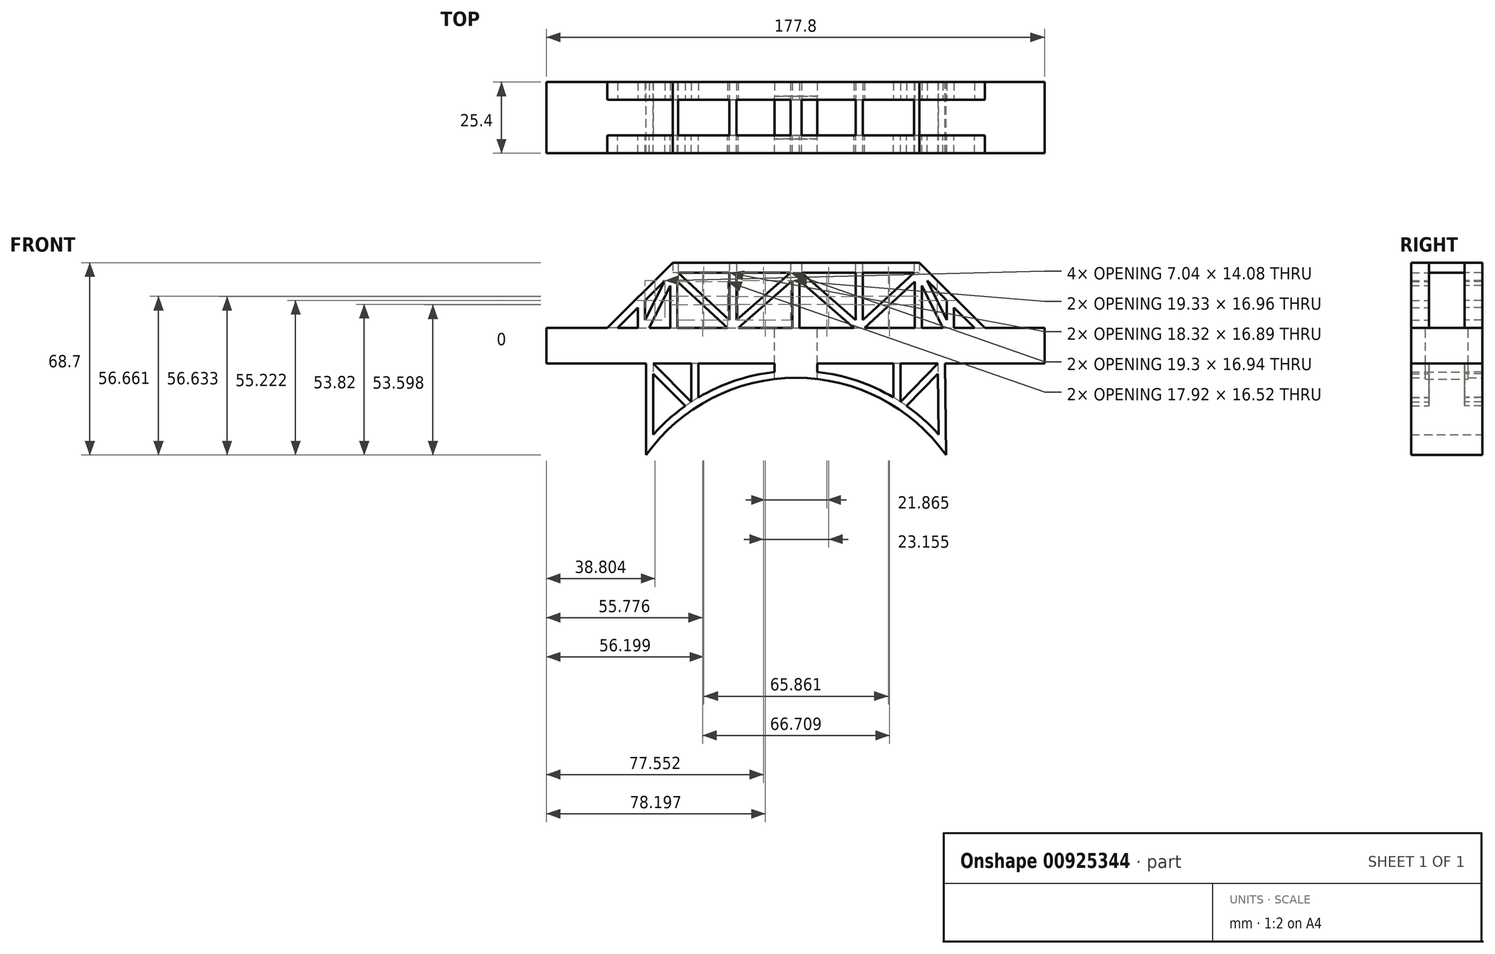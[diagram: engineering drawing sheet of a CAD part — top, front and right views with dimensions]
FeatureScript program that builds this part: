
annotation { "Feature Type Name" : "Feature", "Feature Type Description" : "" }
export const myFeature = defineFeature(function(context is Context, id is Id, definition is map)
    precondition{}
    {
        {
            var Q0;
            Q0=qCreatedBy(makeId("Front.planeOp"),FACE);
            var sketch = newSketch(context, id + "F0", { "sketchPlane" : qUnion([Q0])});
            skLineSegment(sketch, "E0.bottom", {"start": v(-63.73, 4.53) * mm, "end": v(63.73, 4.53) * mm});
            skLineSegment(sketch, "E1.bottom", {"start": v(-63.73, 4.53) * mm, "end": v(-89.13, 4.53) * mm});
            skLineSegment(sketch, "E1.top", {"start": v(-63.73, -8.17) * mm, "end": v(-89.13, -8.17) * mm});
            skLineSegment(sketch, "E1.left", {"start": v(-63.73, -3.37) * mm, "end": v(-63.73, -8.17) * mm});
            skLineSegment(sketch, "E1.right", {"start": v(-89.13, 4.53) * mm, "end": v(-89.13, -8.17) * mm});
            skPoint(sketch, "E2.oppositeSnap0", {"position": v(-76.43, -8.17) * mm});
            skLineSegment(sketch, "E2.bottom", {"start": v(63.27, 4.53) * mm, "end": v(88.67, 4.53) * mm});
            skLineSegment(sketch, "E2.left", {"start": v(63.27, 4.53) * mm, "end": v(63.27, -8.17) * mm});
            skLineSegment(sketch, "E2.right", {"start": v(88.67, 4.53) * mm, "end": v(88.67, -8.17) * mm});
            skPoint(sketch, "E3", {"position": v(-3.25, -27.46) * mm});
            skPoint(sketch, "E4", {"position": v(-24.97, -27.46) * mm});
            skPoint(sketch, "E5", {"position": v(18.48, -27.46) * mm});
            skPoint(sketch, "E6", {"position": v(0, -8.17) * mm});
            skPoint(sketch, "E7", {"position": v(-22.52, -8.17) * mm});
            skPoint(sketch, "E8", {"position": v(22.52, -8.17) * mm});
            skLineSegment(sketch, "E9", {"start": v(-43.58, -8.17) * mm, "end": v(-43.58, 4.53) * mm});
            skLineSegment(sketch, "E10", {"start": v(-22.52, -8.17) * mm, "end": v(-22.52, 4.53) * mm});
            skLineSegment(sketch, "E11", {"start": v(0, -8.17) * mm, "end": v(0, 4.53) * mm});
            skLineSegment(sketch, "E12", {"start": v(22.52, -8.17) * mm, "end": v(22.52, 4.53) * mm});
            skLineSegment(sketch, "E13", {"start": v(43.58, -8.17) * mm, "end": v(43.58, 4.53) * mm});
            skLineSegment(sketch, "E14", {"start": v(-63.73, 4.53) * mm, "end": v(-63.73, 4.53) * mm});
            skLineSegment(sketch, "E15", {"start": v(-63.73, -3.37) * mm, "end": v(-63.73, 4.53) * mm});
            skLineSegment(sketch, "E16", {"start": v(63.73, 4.53) * mm, "end": v(43.97, 24.3) * mm});
            skLineSegment(sketch, "E17", {"start": v(43.97, 24.3) * mm, "end": v(-43.97, 24.3) * mm});
            skLineSegment(sketch, "E18", {"start": v(-43.97, 24.3) * mm, "end": v(-63.73, 4.53) * mm});
            skLineSegment(sketch, "E19", {"start": v(-53.85, 14.41) * mm, "end": v(-53.85, 4.53) * mm});
            skLineSegment(sketch, "E20", {"start": v(-53.85, 4.53) * mm, "end": v(-43.97, 24.3) * mm});
            skLineSegment(sketch, "E21", {"start": v(53.85, 14.41) * mm, "end": v(53.85, 4.53) * mm});
            skLineSegment(sketch, "E22", {"start": v(43.97, 24.3) * mm, "end": v(53.85, 4.53) * mm});
            skLineSegment(sketch, "E23", {"start": v(43.97, 24.3) * mm, "end": v(22.52, 4.53) * mm});
            skLineSegment(sketch, "E24", {"start": v(0, 24.3) * mm, "end": v(22.52, 4.53) * mm});
            skLineSegment(sketch, "E25", {"start": v(-22.52, 4.53) * mm, "end": v(0, 24.3) * mm});
            skLineSegment(sketch, "E26", {"start": v(-43.97, 24.3) * mm, "end": v(-22.52, 4.53) * mm});
            skLineSegment(sketch, "E27.0", {"start": v(43.58, 22.22) * mm, "end": v(52.43, 4.53) * mm});
            skLineSegment(sketch, "E27.1", {"start": v(43.58, 22.22) * mm, "end": v(24.4, 4.53) * mm});
            skLineSegment(sketch, "E27.2", {"start": v(-52.43, 4.53) * mm, "end": v(-43.58, 22.22) * mm});
            skLineSegment(sketch, "E27.3", {"start": v(-43.58, 22.22) * mm, "end": v(-24.4, 4.53) * mm});
            skLineSegment(sketch, "E27.4", {"start": v(-20.6, 4.53) * mm, "end": v(0, 22.6) * mm});
            skLineSegment(sketch, "E27.5", {"start": v(0, 22.6) * mm, "end": v(20.6, 4.53) * mm});
            skLineSegment(sketch, "E28.0", {"start": v(42.1, 24.3) * mm, "end": v(22.5, 6.24) * mm});
            skLineSegment(sketch, "E28.1", {"start": v(1.93, 24.3) * mm, "end": v(22.5, 6.24) * mm});
            skLineSegment(sketch, "E28.2", {"start": v(-22.5, 6.24) * mm, "end": v(-1.93, 24.3) * mm});
            skLineSegment(sketch, "E28.3", {"start": v(-42.1, 24.3) * mm, "end": v(-22.5, 6.24) * mm});
            skLineSegment(sketch, "E29.0", {"start": v(-43.97, 27.89) * mm, "end": v(-67.32, 4.53) * mm});
            skLineSegment(sketch, "E30", {"start": v(-43.97, 27.89) * mm, "end": v(43.97, 27.89) * mm});
            skLineSegment(sketch, "E31.0", {"start": v(67.32, 4.53) * mm, "end": v(43.97, 27.89) * mm});
            skLineSegment(sketch, "E32", {"start": v(-43.58, 4.53) * mm, "end": v(-43.58, 22.22) * mm});
            skLineSegment(sketch, "E33", {"start": v(43.58, 22.22) * mm, "end": v(43.58, 4.53) * mm});
            skLineSegment(sketch, "E34", {"start": v(0, 22.6) * mm, "end": v(0, 4.53) * mm});
            skLineSegment(sketch, "E35", {"start": v(-22.5, 6.24) * mm, "end": v(-22.5, 24.3) * mm});
            skLineSegment(sketch, "E36", {"start": v(22.5, 6.24) * mm, "end": v(22.5, 24.3) * mm});
            skLineSegment(sketch, "E37.0", {"start": v(-21.23, 7.35) * mm, "end": v(-21.23, 24.3) * mm});
            skLineSegment(sketch, "E38.0", {"start": v(-23.77, 7.4) * mm, "end": v(-23.77, 24.3) * mm});
            skLineSegment(sketch, "E39.0", {"start": v(23.77, 7.4) * mm, "end": v(23.77, 24.3) * mm});
            skLineSegment(sketch, "E40.0", {"start": v(21.23, 7.35) * mm, "end": v(21.23, 24.3) * mm});
            skLineSegment(sketch, "E41.0", {"start": v(-42.31, 4.53) * mm, "end": v(-42.31, 21.05) * mm});
            skLineSegment(sketch, "E42.0", {"start": v(-44.85, 4.53) * mm, "end": v(-44.85, 19.68) * mm});
            skLineSegment(sketch, "E43.0", {"start": v(42.31, 21.05) * mm, "end": v(42.31, 4.53) * mm});
            skLineSegment(sketch, "E44.0", {"start": v(44.85, 19.68) * mm, "end": v(44.85, 4.53) * mm});
            skLineSegment(sketch, "E45", {"start": v(-23.77, 24.3) * mm, "end": v(-21.23, 24.3) * mm});
            skLineSegment(sketch, "E46", {"start": v(-23.77, 7.4) * mm, "end": v(-22.5, 6.24) * mm});
            skLineSegment(sketch, "E47", {"start": v(-22.5, 6.24) * mm, "end": v(-21.23, 7.35) * mm});
            skLineSegment(sketch, "E48.0", {"start": v(-1.27, 21.49) * mm, "end": v(-1.27, 4.52) * mm});
            skLineSegment(sketch, "E49.0", {"start": v(1.27, 21.49) * mm, "end": v(1.27, 4.52) * mm});
            skLineSegment(sketch, "E50.0", {"start": v(-56.39, 11.87) * mm, "end": v(-56.39, 4.53) * mm});
            skLineSegment(sketch, "E51.0", {"start": v(56.39, 11.87) * mm, "end": v(56.39, 4.53) * mm});
            skLineSegment(sketch, "E52.0", {"start": v(46.8, 21.45) * mm, "end": v(53.85, 7.37) * mm});
            skLineSegment(sketch, "E53", {"start": v(-7.62, -8.17) * mm, "end": v(-7.62, 4.53) * mm});
            skLineSegment(sketch, "E54", {"start": v(7.62, -8.17) * mm, "end": v(7.62, 4.53) * mm});
            skLineSegment(sketch, "E55.0", {"start": v(-53.85, 7.37) * mm, "end": v(-46.8, 21.45) * mm});
            skLineSegment(sketch, "E56", {"start": v(-51.03, -8.17) * mm, "end": v(-51.03, -33.57) * mm});
            skLineSegment(sketch, "E57", {"start": v(50.57, -8.17) * mm, "end": v(50.93, -33.45) * mm});
            skArc(sketch, "E58", {"start": v(50.93, -33.45) * mm, "mid": v(-0.08, -10.7) * mm, "end": v(-51.03, -33.57) * mm});
            skLineSegment(sketch, "E59.0", {"start": v(-53.57, -8.17) * mm, "end": v(-53.57, -40.8) * mm});
            skArc(sketch, "E59.1", {"start": v(53.57, -40.8) * mm, "mid": v(0, -13.25) * mm, "end": v(-53.57, -40.8) * mm});
            skLineSegment(sketch, "E59.2", {"start": v(53.1, -8.17) * mm, "end": v(53.57, -40.8) * mm});
            skLineSegment(sketch, "E60", {"start": v(-51.03, -8.17) * mm, "end": v(-37.37, -21.83) * mm});
            skLineSegment(sketch, "E61", {"start": v(-37.37, -21.83) * mm, "end": v(-37.37, -8.17) * mm});
            skLineSegment(sketch, "E62", {"start": v(37.32, -8.14) * mm, "end": v(37.32, -21.8) * mm});
            skLineSegment(sketch, "E63", {"start": v(37.32, -21.8) * mm, "end": v(50.57, -8.17) * mm});
            skLineSegment(sketch, "E64.0", {"start": v(34.78, -8.14) * mm, "end": v(34.78, -20.22) * mm});
            skLineSegment(sketch, "E65.0", {"start": v(39.46, -23.24) * mm, "end": v(50.62, -11.76) * mm});
            skLineSegment(sketch, "E66.0", {"start": v(-34.83, -20.25) * mm, "end": v(-34.83, -8.17) * mm});
            skLineSegment(sketch, "E67.0", {"start": v(-51.03, -11.76) * mm, "end": v(-39.51, -23.28) * mm});
            skLineSegment(sketch, "E68", {"start": v(-22.52, -8.17) * mm, "end": v(-17.66, -13.03) * mm});
            skLineSegment(sketch, "E69", {"start": v(22.52, -8.17) * mm, "end": v(17.66, -13.03) * mm});
            skLineSegment(sketch, "E70", {"start": v(-7.62, -8.17) * mm, "end": v(-7.62, -11.14) * mm});
            skLineSegment(sketch, "E71", {"start": v(7.62, -8.17) * mm, "end": v(7.62, -11.14) * mm});
            skLineSegment(sketch, "E72", {"start": v(88.67, -8.17) * mm, "end": v(-63.73, -8.17) * mm});
            skSolve(sketch);
        }
        {
            var Q0;
            Q0=makeQuery(id+"F0.imprint","IMPRINT",FACE,{"disambiguationData":[TD([[makeQuery(id+"F0.imprint","IMPRINT",EDGE,{"derivedFrom":sQuery(id+"F0.wireOp",EDGE,"E1.top")}),-1.0]])]});
            var Q1;
            {var subQ0=sQuery(id+"F0.wireOp",EDGE,"E2.left");Q1=makeQuery(id+"F0.imprint","IMPRINT",FACE,{"disambiguationData":[TD([[makeQuery(id+"F0.imprint","IMPRINT",EDGE,{"derivedFrom":subQ0}),1.0]])]});}
            extrude(context, id + "F1", {"entities" : qUnion([Q0, Q1]), "endBound" : BoundingType.SYMMETRIC, "depth" : 12.7 * mm, "offsetDistance" : 25.4 * mm});
        }
        {
            var Q0;
            {var subQ6=sQuery(id+"F0.wireOp",EDGE,"E1.left");Q0=makeQuery(id+"F0.imprint","IMPRINT",FACE,{"disambiguationData":[TD([[makeQuery(id+"F0.imprint","IMPRINT",EDGE,{"derivedFrom":subQ6}),1.0]])]});}
            var Q1;
            {var subQ0=sQuery(id+"F0.wireOp",EDGE,"E9");Q1=makeQuery(id+"F0.imprint","IMPRINT",FACE,{"disambiguationData":[TD([[makeQuery(id+"F0.imprint","IMPRINT",EDGE,{"derivedFrom":subQ0}),-1.0]])]});}
            var Q2;
            {var subQ0=sQuery(id+"F0.wireOp",EDGE,"E12");Q2=makeQuery(id+"F0.imprint","IMPRINT",FACE,{"disambiguationData":[TD([[makeQuery(id+"F0.imprint","IMPRINT",EDGE,{"derivedFrom":subQ0}),-1.0]])]});}
            var Q3;
            {var subQ4=sQuery(id+"F0.wireOp",EDGE,"E2.left");Q3=makeQuery(id+"F0.imprint","IMPRINT",FACE,{"disambiguationData":[TD([[makeQuery(id+"F0.imprint","IMPRINT",EDGE,{"derivedFrom":subQ4}),-1.0]])]});}
            var Q4;
            {var subQ1=sQuery(id+"F0.wireOp",EDGE,"E10");Q4=makeQuery(id+"F0.imprint","IMPRINT",FACE,{"disambiguationData":[TD([[makeQuery(id+"F0.imprint","IMPRINT",EDGE,{"derivedFrom":subQ1}),-1.0]])]});}
            var Q5;
            {var subQ0=sQuery(id+"F0.wireOp",EDGE,"E12");Q5=makeQuery(id+"F0.imprint","IMPRINT",FACE,{"disambiguationData":[TD([[makeQuery(id+"F0.imprint","IMPRINT",EDGE,{"derivedFrom":subQ0}),1.0]])]});}
            extrude(context, id + "F2", {"entities" : qUnion([Q0, Q1, Q2, Q3, Q4, Q5]), "operationType" : NewBodyOperationType.ADD, "endBound" : BoundingType.SYMMETRIC, "depth" : 12.7 * mm, "offsetDistance" : 25.4 * mm});
        }
        {
            var Q0;
            {var subQ6=sQuery(id+"F0.wireOp",EDGE,"E1.left");Q0=makeQuery(id+"F0.imprint","IMPRINT",FACE,{"disambiguationData":[TD([[makeQuery(id+"F0.imprint","IMPRINT",EDGE,{"derivedFrom":subQ6}),1.0]])]});}
            var Q1;
            {var subQ0=sQuery(id+"F0.wireOp",EDGE,"E9");Q1=makeQuery(id+"F0.imprint","IMPRINT",FACE,{"disambiguationData":[TD([[makeQuery(id+"F0.imprint","IMPRINT",EDGE,{"derivedFrom":subQ0}),-1.0]])]});}
            var Q2;
            {var subQ1=sQuery(id+"F0.wireOp",EDGE,"E10");Q2=makeQuery(id+"F0.imprint","IMPRINT",FACE,{"disambiguationData":[TD([[makeQuery(id+"F0.imprint","IMPRINT",EDGE,{"derivedFrom":subQ1}),-1.0]])]});}
            var Q3;
            {var subQ1=sQuery(id+"F0.wireOp",EDGE,"E11");Q3=makeQuery(id+"F0.imprint","IMPRINT",FACE,{"disambiguationData":[TD([[makeQuery(id+"F0.imprint","IMPRINT",EDGE,{"derivedFrom":subQ1}),-1.0]])]});}
            var Q4;
            {var subQ0=sQuery(id+"F0.wireOp",EDGE,"E12");Q4=makeQuery(id+"F0.imprint","IMPRINT",FACE,{"disambiguationData":[TD([[makeQuery(id+"F0.imprint","IMPRINT",EDGE,{"derivedFrom":subQ0}),-1.0]])]});}
            var Q5;
            {var subQ4=sQuery(id+"F0.wireOp",EDGE,"E2.left");Q5=makeQuery(id+"F0.imprint","IMPRINT",FACE,{"disambiguationData":[TD([[makeQuery(id+"F0.imprint","IMPRINT",EDGE,{"derivedFrom":subQ4}),-1.0]])]});}
            extrude(context, id + "F3", {"entities" : qUnion([Q0, Q1, Q2, Q3, Q4, Q5]), "operationType" : NewBodyOperationType.ADD, "endBound" : BoundingType.SYMMETRIC, "depth" : 7.62 * mm, "offsetDistance" : 25.4 * mm});
        }
        {
            var Q0;
            {var subQ1=sQuery(id+"F0.wireOp",EDGE,"E24");Q0=makeQuery(id+"F0.imprint","IMPRINT",FACE,{"disambiguationData":[TD([[makeQuery(id+"F0.imprint","IMPRINT",EDGE,{"derivedFrom":subQ1}),-1.0]])]});}
            var Q1;
            {var subQ0=sQuery(id+"F0.wireOp",EDGE,"E25");Q1=makeQuery(id+"F0.imprint","IMPRINT",FACE,{"disambiguationData":[TD([[makeQuery(id+"F0.imprint","IMPRINT",EDGE,{"derivedFrom":subQ0}),1.0]])]});}
            var Q2;
            {var subQ0=sQuery(id+"F0.wireOp",EDGE,"E25");Q2=makeQuery(id+"F0.imprint","IMPRINT",FACE,{"disambiguationData":[TD([[makeQuery(id+"F0.imprint","IMPRINT",EDGE,{"derivedFrom":subQ0}),1.0]])]});}
            var Q3;
            {var subQ1=sQuery(id+"F0.wireOp",EDGE,"E20");Q3=makeQuery(id+"F0.imprint","IMPRINT",FACE,{"disambiguationData":[TD([[makeQuery(id+"F0.imprint","IMPRINT",EDGE,{"derivedFrom":subQ1}),-1.0]])]});}
            var Q4;
            {var subQ1=sQuery(id+"F0.wireOp",EDGE,"E20");Q4=makeQuery(id+"F0.imprint","IMPRINT",FACE,{"disambiguationData":[TD([[makeQuery(id+"F0.imprint","IMPRINT",EDGE,{"derivedFrom":subQ1}),-1.0]])]});}
            var Q5;
            {var subQ1=sQuery(id+"F0.wireOp",EDGE,"E23");Q5=makeQuery(id+"F0.imprint","IMPRINT",FACE,{"disambiguationData":[TD([[makeQuery(id+"F0.imprint","IMPRINT",EDGE,{"derivedFrom":subQ1}),-1.0]])]});}
            var Q6;
            {var subQ1=sQuery(id+"F0.wireOp",EDGE,"E24");Q6=makeQuery(id+"F0.imprint","IMPRINT",FACE,{"disambiguationData":[TD([[makeQuery(id+"F0.imprint","IMPRINT",EDGE,{"derivedFrom":subQ1}),-1.0]])]});}
            var Q7;
            {var subQ1=sQuery(id+"F0.wireOp",EDGE,"E22");Q7=makeQuery(id+"F0.imprint","IMPRINT",FACE,{"disambiguationData":[TD([[makeQuery(id+"F0.imprint","IMPRINT",EDGE,{"derivedFrom":subQ1}),-1.0]])]});}
            var Q8;
            {var subQ1=sQuery(id+"F0.wireOp",EDGE,"E23");Q8=makeQuery(id+"F0.imprint","IMPRINT",FACE,{"disambiguationData":[TD([[makeQuery(id+"F0.imprint","IMPRINT",EDGE,{"derivedFrom":subQ1}),-1.0]])]});}
            var Q9;
            {var subQ1=sQuery(id+"F0.wireOp",EDGE,"E22");Q9=makeQuery(id+"F0.imprint","IMPRINT",FACE,{"disambiguationData":[TD([[makeQuery(id+"F0.imprint","IMPRINT",EDGE,{"derivedFrom":subQ1}),-1.0]])]});}
            var Q10;
            {var subQ0=sQuery(id+"F0.wireOp",EDGE,"E15");var subQ1=sQuery(id+"F0.wireOp",EDGE,"E1.left");Q10=makeQuery(id+"F2.boolean.opBoolean","MERGE",FACE,{"derivedFrom":[makeQuery(id+"F1.opExtrude","CAP_FACE",FACE,{"disambiguationData":[OSD([sQuery(id+"F0.wireOp",EDGE,"E1.bottom"),sQuery(id+"F0.wireOp",EDGE,"E1.top"),subQ1,sQuery(id+"F0.wireOp",EDGE,"E1.right"),subQ0])],"isStart":false}),makeQuery(id+"F2.opExtrude","CAP_FACE",FACE,{"disambiguationData":[OSD([sQuery(id+"F0.wireOp",EDGE,"E0.bottom"),subQ1,subQ0,sQuery(id+"F0.wireOp",EDGE,"E53"),sQuery(id+"F0.wireOp",EDGE,"E72")])],"isStart":false})]});}
            extrude(context, id + "F4", {"entities" : qUnion([Q0, Q1, Q2, Q3, Q4, Q5, Q6, Q7, Q8, Q9]), "operationType" : NewBodyOperationType.ADD, "endBound" : BoundingType.UP_TO_SURFACE, "depth" : 12.7 * mm, "endBoundEntityFace" : qUnion([Q10]), "offsetDistance" : 25.4 * mm});
        }
        {
            var Q0;
            {var subQ28=sQuery(id+"F0.wireOp",EDGE,"E29.0");Q0=makeQuery(id+"F0.imprint","IMPRINT",FACE,{"disambiguationData":[TD([[makeQuery(id+"F0.imprint","IMPRINT",EDGE,{"derivedFrom":subQ28}),1.0]])]});}
            var Q1;
            {var subQ0=sQuery(id+"F0.wireOp",EDGE,"E0.bottom");var subQ1=sQuery(id+"F0.wireOp",EDGE,"E15");var subQ2=sQuery(id+"F0.wireOp",EDGE,"E1.left");Q1=makeQuery(id+"F4.boolean.opBoolean","MERGE",FACE,{"derivedFrom":[makeQuery(id+"F2.boolean.opBoolean","MERGE",FACE,{"derivedFrom":[makeQuery(id+"F1.opExtrude","CAP_FACE",FACE,{"disambiguationData":[OSD([sQuery(id+"F0.wireOp",EDGE,"E1.bottom"),sQuery(id+"F0.wireOp",EDGE,"E1.top"),subQ2,sQuery(id+"F0.wireOp",EDGE,"E1.right"),subQ1])],"isStart":false}),makeQuery(id+"F2.opExtrude","CAP_FACE",FACE,{"disambiguationData":[OSD([subQ0,subQ2,subQ1,sQuery(id+"F0.wireOp",EDGE,"E53"),sQuery(id+"F0.wireOp",EDGE,"E72")])],"isStart":false})]}),makeQuery(id+"F4.opExtrude","CAP_FACE",FACE,{"disambiguationData":[OSD([subQ0,sQuery(id+"F0.wireOp",EDGE,"E17"),sQuery(id+"F0.wireOp",EDGE,"E20"),sQuery(id+"F0.wireOp",EDGE,"E22"),sQuery(id+"F0.wireOp",EDGE,"E27.0"),sQuery(id+"F0.wireOp",EDGE,"E27.1"),sQuery(id+"F0.wireOp",EDGE,"E27.2"),sQuery(id+"F0.wireOp",EDGE,"E27.3"),sQuery(id+"F0.wireOp",EDGE,"E27.4"),sQuery(id+"F0.wireOp",EDGE,"E27.5"),sQuery(id+"F0.wireOp",EDGE,"E28.0"),sQuery(id+"F0.wireOp",EDGE,"E28.1"),sQuery(id+"F0.wireOp",EDGE,"E28.2"),sQuery(id+"F0.wireOp",EDGE,"E28.3")])],"isStart":false})]});}
            extrude(context, id + "F5", {"entities" : qUnion([Q0]), "operationType" : NewBodyOperationType.ADD, "endBound" : BoundingType.UP_TO_SURFACE, "depth" : 12.7 * mm, "endBoundEntityFace" : qUnion([Q1]), "offsetDistance" : 25.4 * mm});
        }
        {
            var Q0;
            {var subQ0=sQuery(id+"F0.wireOp",EDGE,"E35");Q0=makeQuery(id+"F0.imprint","IMPRINT",FACE,{"disambiguationData":[TD([[makeQuery(id+"F0.imprint","IMPRINT",EDGE,{"derivedFrom":subQ0}),1.0]])]});}
            var Q1;
            {var subQ0=sQuery(id+"F0.wireOp",EDGE,"E35");Q1=makeQuery(id+"F0.imprint","IMPRINT",FACE,{"disambiguationData":[TD([[makeQuery(id+"F0.imprint","IMPRINT",EDGE,{"derivedFrom":subQ0}),-1.0]])]});}
            var Q2;
            {var subQ0=sQuery(id+"F0.wireOp",EDGE,"E32");Q2=makeQuery(id+"F0.imprint","IMPRINT",FACE,{"disambiguationData":[TD([[makeQuery(id+"F0.imprint","IMPRINT",EDGE,{"derivedFrom":subQ0}),-1.0]])]});}
            var Q3;
            {var subQ0=sQuery(id+"F0.wireOp",EDGE,"E32");Q3=makeQuery(id+"F0.imprint","IMPRINT",FACE,{"disambiguationData":[TD([[makeQuery(id+"F0.imprint","IMPRINT",EDGE,{"derivedFrom":subQ0}),1.0]])]});}
            var Q4;
            {var subQ0=sQuery(id+"F0.wireOp",EDGE,"E36");Q4=makeQuery(id+"F0.imprint","IMPRINT",FACE,{"disambiguationData":[TD([[makeQuery(id+"F0.imprint","IMPRINT",EDGE,{"derivedFrom":subQ0}),1.0]])]});}
            var Q5;
            {var subQ0=sQuery(id+"F0.wireOp",EDGE,"E36");Q5=makeQuery(id+"F0.imprint","IMPRINT",FACE,{"disambiguationData":[TD([[makeQuery(id+"F0.imprint","IMPRINT",EDGE,{"derivedFrom":subQ0}),-1.0]])]});}
            var Q6;
            {var subQ0=sQuery(id+"F0.wireOp",EDGE,"E33");Q6=makeQuery(id+"F0.imprint","IMPRINT",FACE,{"disambiguationData":[TD([[makeQuery(id+"F0.imprint","IMPRINT",EDGE,{"derivedFrom":subQ0}),1.0]])]});}
            var Q7;
            {var subQ0=sQuery(id+"F0.wireOp",EDGE,"E33");Q7=makeQuery(id+"F0.imprint","IMPRINT",FACE,{"disambiguationData":[TD([[makeQuery(id+"F0.imprint","IMPRINT",EDGE,{"derivedFrom":subQ0}),-1.0]])]});}
            var Q8;
            {var subQ0=sQuery(id+"F0.wireOp",EDGE,"E17");var subQ1=sQuery(id+"F0.wireOp",EDGE,"E1.bottom");var subQ2=sQuery(id+"F0.wireOp",EDGE,"E0.bottom");var subQ3=sQuery(id+"F0.wireOp",EDGE,"E15");var subQ4=sQuery(id+"F0.wireOp",EDGE,"E1.left");Q8=makeQuery(id+"F5.boolean.opBoolean","MERGE",FACE,{"derivedFrom":[makeQuery(id+"F4.boolean.opBoolean","MERGE",FACE,{"derivedFrom":[makeQuery(id+"F2.boolean.opBoolean","MERGE",FACE,{"derivedFrom":[makeQuery(id+"F1.opExtrude","CAP_FACE",FACE,{"disambiguationData":[OSD([subQ1,sQuery(id+"F0.wireOp",EDGE,"E1.top"),subQ4,sQuery(id+"F0.wireOp",EDGE,"E1.right"),subQ3])],"isStart":false}),makeQuery(id+"F2.opExtrude","CAP_FACE",FACE,{"disambiguationData":[OSD([subQ2,subQ4,subQ3,sQuery(id+"F0.wireOp",EDGE,"E53"),sQuery(id+"F0.wireOp",EDGE,"E72")])],"isStart":false})]}),makeQuery(id+"F4.opExtrude","CAP_FACE",FACE,{"disambiguationData":[OSD([subQ2,subQ0,sQuery(id+"F0.wireOp",EDGE,"E20"),sQuery(id+"F0.wireOp",EDGE,"E22"),sQuery(id+"F0.wireOp",EDGE,"E27.0"),sQuery(id+"F0.wireOp",EDGE,"E27.1"),sQuery(id+"F0.wireOp",EDGE,"E27.2"),sQuery(id+"F0.wireOp",EDGE,"E27.3"),sQuery(id+"F0.wireOp",EDGE,"E27.4"),sQuery(id+"F0.wireOp",EDGE,"E27.5"),sQuery(id+"F0.wireOp",EDGE,"E28.0"),sQuery(id+"F0.wireOp",EDGE,"E28.1"),sQuery(id+"F0.wireOp",EDGE,"E28.2"),sQuery(id+"F0.wireOp",EDGE,"E28.3")])],"isStart":false})]}),makeQuery(id+"F5.opExtrude","CAP_FACE",FACE,{"disambiguationData":[OSD([subQ1,sQuery(id+"F0.wireOp",EDGE,"E2.bottom"),sQuery(id+"F0.wireOp",EDGE,"E16"),subQ0,sQuery(id+"F0.wireOp",EDGE,"E18"),sQuery(id+"F0.wireOp",EDGE,"E29.0"),sQuery(id+"F0.wireOp",EDGE,"E30"),sQuery(id+"F0.wireOp",EDGE,"E31.0")])],"isStart":false})]});}
            extrude(context, id + "F6", {"entities" : qUnion([Q0, Q1, Q2, Q3, Q4, Q5, Q6, Q7]), "operationType" : NewBodyOperationType.ADD, "endBound" : BoundingType.UP_TO_SURFACE, "depth" : 12.7 * mm, "endBoundEntityFace" : qUnion([Q8]), "offsetDistance" : 25.4 * mm});
        }
        {
            var Q0;
            {var subQ0=sQuery(id+"F0.wireOp",EDGE,"E34");Q0=makeQuery(id+"F0.imprint","IMPRINT",FACE,{"disambiguationData":[TD([[makeQuery(id+"F0.imprint","IMPRINT",EDGE,{"derivedFrom":subQ0}),-1.0]])]});}
            var Q1;
            {var subQ0=sQuery(id+"F0.wireOp",EDGE,"E34");Q1=makeQuery(id+"F0.imprint","IMPRINT",FACE,{"disambiguationData":[TD([[makeQuery(id+"F0.imprint","IMPRINT",EDGE,{"derivedFrom":subQ0}),1.0]])]});}
            var Q2;
            {var subQ0=sQuery(id+"F0.wireOp",EDGE,"E28.3");var subQ1=sQuery(id+"F0.wireOp",EDGE,"E28.2");var subQ2=sQuery(id+"F0.wireOp",EDGE,"E17");var subQ3=sQuery(id+"F0.wireOp",EDGE,"E28.1");var subQ4=sQuery(id+"F0.wireOp",EDGE,"E28.0");var subQ5=sQuery(id+"F0.wireOp",EDGE,"E27.1");var subQ6=sQuery(id+"F0.wireOp",EDGE,"E27.0");var subQ7=sQuery(id+"F0.wireOp",EDGE,"E0.bottom");var subQ8=sQuery(id+"F0.wireOp",EDGE,"E27.3");var subQ9=sQuery(id+"F0.wireOp",EDGE,"E27.2");var subQ10=sQuery(id+"F0.wireOp",EDGE,"E2.bottom");var subQ11=sQuery(id+"F0.wireOp",EDGE,"E1.bottom");var subQ12=sQuery(id+"F0.wireOp",EDGE,"E72");var subQ13=sQuery(id+"F0.wireOp",EDGE,"E15");var subQ14=sQuery(id+"F0.wireOp",EDGE,"E1.left");var subQ15=sQuery(id+"F0.wireOp",EDGE,"E2.left");Q2=makeQuery(id+"F6.boolean.opBoolean","MERGE",FACE,{"derivedFrom":[makeQuery(id+"F2.boolean.opBoolean","MERGE",FACE,{"derivedFrom":[makeQuery(id+"F1.opExtrude","CAP_FACE",FACE,{"disambiguationData":[OSD([subQ7,subQ10,subQ15,sQuery(id+"F0.wireOp",EDGE,"E2.right"),subQ12])],"isStart":false}),makeQuery(id+"F2.opExtrude","CAP_FACE",FACE,{"disambiguationData":[OSD([subQ7,subQ15,sQuery(id+"F0.wireOp",EDGE,"E54"),subQ12])],"isStart":false})]}),makeQuery(id+"F5.boolean.opBoolean","MERGE",FACE,{"derivedFrom":[makeQuery(id+"F4.boolean.opBoolean","MERGE",FACE,{"derivedFrom":[makeQuery(id+"F2.boolean.opBoolean","MERGE",FACE,{"derivedFrom":[makeQuery(id+"F1.opExtrude","CAP_FACE",FACE,{"disambiguationData":[OSD([subQ11,sQuery(id+"F0.wireOp",EDGE,"E1.top"),subQ14,sQuery(id+"F0.wireOp",EDGE,"E1.right"),subQ13])],"isStart":false}),makeQuery(id+"F2.opExtrude","CAP_FACE",FACE,{"disambiguationData":[OSD([subQ7,subQ14,subQ13,sQuery(id+"F0.wireOp",EDGE,"E53"),subQ12])],"isStart":false})]}),makeQuery(id+"F4.opExtrude","CAP_FACE",FACE,{"disambiguationData":[OSD([subQ7,subQ2,sQuery(id+"F0.wireOp",EDGE,"E20"),sQuery(id+"F0.wireOp",EDGE,"E22"),subQ6,subQ5,subQ9,subQ8,sQuery(id+"F0.wireOp",EDGE,"E27.4"),sQuery(id+"F0.wireOp",EDGE,"E27.5"),subQ4,subQ3,subQ1,subQ0])],"isStart":false})]}),makeQuery(id+"F5.opExtrude","CAP_FACE",FACE,{"disambiguationData":[OSD([subQ11,subQ10,sQuery(id+"F0.wireOp",EDGE,"E16"),subQ2,sQuery(id+"F0.wireOp",EDGE,"E18"),sQuery(id+"F0.wireOp",EDGE,"E29.0"),sQuery(id+"F0.wireOp",EDGE,"E30"),sQuery(id+"F0.wireOp",EDGE,"E31.0")])],"isStart":false})]}),makeQuery(id+"F6.opExtrude","CAP_FACE",FACE,{"disambiguationData":[OSD([subQ7,subQ9,subQ8,sQuery(id+"F0.wireOp",EDGE,"E41.0"),sQuery(id+"F0.wireOp",EDGE,"E42.0")])],"isStart":false}),makeQuery(id+"F6.opExtrude","CAP_FACE",FACE,{"disambiguationData":[OSD([subQ7,subQ6,subQ5,sQuery(id+"F0.wireOp",EDGE,"E43.0"),sQuery(id+"F0.wireOp",EDGE,"E44.0")])],"isStart":false}),makeQuery(id+"F6.opExtrude","CAP_FACE",FACE,{"disambiguationData":[OSD([subQ2,subQ4,subQ3,sQuery(id+"F0.wireOp",EDGE,"E39.0"),sQuery(id+"F0.wireOp",EDGE,"E40.0")])],"isStart":false}),makeQuery(id+"F6.opExtrude","CAP_FACE",FACE,{"disambiguationData":[OSD([subQ2,subQ1,subQ0,sQuery(id+"F0.wireOp",EDGE,"E37.0"),sQuery(id+"F0.wireOp",EDGE,"E38.0")])],"isStart":false})]});}
            extrude(context, id + "F7", {"entities" : qUnion([Q0, Q1]), "operationType" : NewBodyOperationType.ADD, "endBound" : BoundingType.UP_TO_SURFACE, "depth" : 12.7 * mm, "endBoundEntityFace" : qUnion([Q2]), "offsetDistance" : 25.4 * mm});
        }
        {
            var Q0;
            {var subQ6=sQuery(id+"F0.wireOp",EDGE,"E51.0");Q0=makeQuery(id+"F0.imprint","IMPRINT",FACE,{"disambiguationData":[TD([[makeQuery(id+"F0.imprint","IMPRINT",EDGE,{"derivedFrom":subQ6}),-1.0]])]});}
            var Q1;
            {var subQ4=sQuery(id+"F0.wireOp",EDGE,"E50.0");Q1=makeQuery(id+"F0.imprint","IMPRINT",FACE,{"disambiguationData":[TD([[makeQuery(id+"F0.imprint","IMPRINT",EDGE,{"derivedFrom":subQ4}),1.0]])]});}
            var Q2;
            {var subQ0=sQuery(id+"F0.wireOp",EDGE,"E27.5");var subQ1=sQuery(id+"F0.wireOp",EDGE,"E27.4");var subQ2=sQuery(id+"F0.wireOp",EDGE,"E0.bottom");var subQ3=sQuery(id+"F0.wireOp",EDGE,"E28.3");var subQ4=sQuery(id+"F0.wireOp",EDGE,"E28.2");var subQ5=sQuery(id+"F0.wireOp",EDGE,"E17");var subQ6=sQuery(id+"F0.wireOp",EDGE,"E28.1");var subQ7=sQuery(id+"F0.wireOp",EDGE,"E28.0");var subQ8=sQuery(id+"F0.wireOp",EDGE,"E27.1");var subQ9=sQuery(id+"F0.wireOp",EDGE,"E27.0");var subQ10=sQuery(id+"F0.wireOp",EDGE,"E27.3");var subQ11=sQuery(id+"F0.wireOp",EDGE,"E27.2");var subQ12=sQuery(id+"F0.wireOp",EDGE,"E2.bottom");var subQ13=sQuery(id+"F0.wireOp",EDGE,"E1.bottom");var subQ14=sQuery(id+"F0.wireOp",EDGE,"E72");var subQ15=sQuery(id+"F0.wireOp",EDGE,"E15");var subQ16=sQuery(id+"F0.wireOp",EDGE,"E1.left");var subQ17=sQuery(id+"F0.wireOp",EDGE,"E2.left");Q2=makeQuery(id+"F7.boolean.opBoolean","MERGE",FACE,{"derivedFrom":[makeQuery(id+"F6.boolean.opBoolean","MERGE",FACE,{"derivedFrom":[makeQuery(id+"F2.boolean.opBoolean","MERGE",FACE,{"derivedFrom":[makeQuery(id+"F1.opExtrude","CAP_FACE",FACE,{"disambiguationData":[OSD([subQ2,subQ12,subQ17,sQuery(id+"F0.wireOp",EDGE,"E2.right"),subQ14])],"isStart":false}),makeQuery(id+"F2.opExtrude","CAP_FACE",FACE,{"disambiguationData":[OSD([subQ2,subQ17,sQuery(id+"F0.wireOp",EDGE,"E54"),subQ14])],"isStart":false})]}),makeQuery(id+"F5.boolean.opBoolean","MERGE",FACE,{"derivedFrom":[makeQuery(id+"F4.boolean.opBoolean","MERGE",FACE,{"derivedFrom":[makeQuery(id+"F2.boolean.opBoolean","MERGE",FACE,{"derivedFrom":[makeQuery(id+"F1.opExtrude","CAP_FACE",FACE,{"disambiguationData":[OSD([subQ13,sQuery(id+"F0.wireOp",EDGE,"E1.top"),subQ16,sQuery(id+"F0.wireOp",EDGE,"E1.right"),subQ15])],"isStart":false}),makeQuery(id+"F2.opExtrude","CAP_FACE",FACE,{"disambiguationData":[OSD([subQ2,subQ16,subQ15,sQuery(id+"F0.wireOp",EDGE,"E53"),subQ14])],"isStart":false})]}),makeQuery(id+"F4.opExtrude","CAP_FACE",FACE,{"disambiguationData":[OSD([subQ2,subQ5,sQuery(id+"F0.wireOp",EDGE,"E20"),sQuery(id+"F0.wireOp",EDGE,"E22"),subQ9,subQ8,subQ11,subQ10,subQ1,subQ0,subQ7,subQ6,subQ4,subQ3])],"isStart":false})]}),makeQuery(id+"F5.opExtrude","CAP_FACE",FACE,{"disambiguationData":[OSD([subQ13,subQ12,sQuery(id+"F0.wireOp",EDGE,"E16"),subQ5,sQuery(id+"F0.wireOp",EDGE,"E18"),sQuery(id+"F0.wireOp",EDGE,"E29.0"),sQuery(id+"F0.wireOp",EDGE,"E30"),sQuery(id+"F0.wireOp",EDGE,"E31.0")])],"isStart":false})]}),makeQuery(id+"F6.opExtrude","CAP_FACE",FACE,{"disambiguationData":[OSD([subQ2,subQ11,subQ10,sQuery(id+"F0.wireOp",EDGE,"E41.0"),sQuery(id+"F0.wireOp",EDGE,"E42.0")])],"isStart":false}),makeQuery(id+"F6.opExtrude","CAP_FACE",FACE,{"disambiguationData":[OSD([subQ2,subQ9,subQ8,sQuery(id+"F0.wireOp",EDGE,"E43.0"),sQuery(id+"F0.wireOp",EDGE,"E44.0")])],"isStart":false}),makeQuery(id+"F6.opExtrude","CAP_FACE",FACE,{"disambiguationData":[OSD([subQ5,subQ7,subQ6,sQuery(id+"F0.wireOp",EDGE,"E39.0"),sQuery(id+"F0.wireOp",EDGE,"E40.0")])],"isStart":false}),makeQuery(id+"F6.opExtrude","CAP_FACE",FACE,{"disambiguationData":[OSD([subQ5,subQ4,subQ3,sQuery(id+"F0.wireOp",EDGE,"E37.0"),sQuery(id+"F0.wireOp",EDGE,"E38.0")])],"isStart":false})]}),makeQuery(id+"F7.opExtrude","CAP_FACE",FACE,{"disambiguationData":[OSD([subQ2,subQ1,subQ0,sQuery(id+"F0.wireOp",EDGE,"E48.0"),sQuery(id+"F0.wireOp",EDGE,"E49.0")])],"isStart":false})]});}
            extrude(context, id + "F8", {"entities" : qUnion([Q0, Q1]), "operationType" : NewBodyOperationType.ADD, "endBound" : BoundingType.UP_TO_SURFACE, "depth" : 12.7 * mm, "endBoundEntityFace" : qUnion([Q2]), "offsetDistance" : 25.4 * mm});
        }
        {
            var Q0;
            {var subQ0=sQuery(id+"F0.wireOp",EDGE,"E22");Q0=makeQuery(id+"F0.imprint","IMPRINT",FACE,{"disambiguationData":[TD([[makeQuery(id+"F0.imprint","IMPRINT",EDGE,{"derivedFrom":subQ0}),1.0]])]});}
            var Q1;
            {var subQ0=sQuery(id+"F0.wireOp",EDGE,"E18");var subQ1=sQuery(id+"F0.wireOp",EDGE,"E0.bottom");var subQ2=sQuery(id+"F0.wireOp",EDGE,"E16");var subQ3=sQuery(id+"F0.wireOp",EDGE,"E27.5");var subQ4=sQuery(id+"F0.wireOp",EDGE,"E27.4");var subQ5=sQuery(id+"F0.wireOp",EDGE,"E28.3");var subQ6=sQuery(id+"F0.wireOp",EDGE,"E28.2");var subQ7=sQuery(id+"F0.wireOp",EDGE,"E17");var subQ8=sQuery(id+"F0.wireOp",EDGE,"E28.1");var subQ9=sQuery(id+"F0.wireOp",EDGE,"E28.0");var subQ10=sQuery(id+"F0.wireOp",EDGE,"E27.1");var subQ11=sQuery(id+"F0.wireOp",EDGE,"E27.0");var subQ12=sQuery(id+"F0.wireOp",EDGE,"E27.3");var subQ13=sQuery(id+"F0.wireOp",EDGE,"E27.2");var subQ14=sQuery(id+"F0.wireOp",EDGE,"E2.bottom");var subQ15=sQuery(id+"F0.wireOp",EDGE,"E1.bottom");var subQ16=sQuery(id+"F0.wireOp",EDGE,"E72");var subQ17=sQuery(id+"F0.wireOp",EDGE,"E15");var subQ18=sQuery(id+"F0.wireOp",EDGE,"E1.left");var subQ19=sQuery(id+"F0.wireOp",EDGE,"E2.left");Q1=makeQuery(id+"F8.boolean.opBoolean","MERGE",FACE,{"derivedFrom":[makeQuery(id+"F7.boolean.opBoolean","MERGE",FACE,{"derivedFrom":[makeQuery(id+"F6.boolean.opBoolean","MERGE",FACE,{"derivedFrom":[makeQuery(id+"F2.boolean.opBoolean","MERGE",FACE,{"derivedFrom":[makeQuery(id+"F1.opExtrude","CAP_FACE",FACE,{"disambiguationData":[OSD([subQ1,subQ14,subQ19,sQuery(id+"F0.wireOp",EDGE,"E2.right"),subQ16])],"isStart":false}),makeQuery(id+"F2.opExtrude","CAP_FACE",FACE,{"disambiguationData":[OSD([subQ1,subQ19,sQuery(id+"F0.wireOp",EDGE,"E54"),subQ16])],"isStart":false})]}),makeQuery(id+"F5.boolean.opBoolean","MERGE",FACE,{"derivedFrom":[makeQuery(id+"F4.boolean.opBoolean","MERGE",FACE,{"derivedFrom":[makeQuery(id+"F2.boolean.opBoolean","MERGE",FACE,{"derivedFrom":[makeQuery(id+"F1.opExtrude","CAP_FACE",FACE,{"disambiguationData":[OSD([subQ15,sQuery(id+"F0.wireOp",EDGE,"E1.top"),subQ18,sQuery(id+"F0.wireOp",EDGE,"E1.right"),subQ17])],"isStart":false}),makeQuery(id+"F2.opExtrude","CAP_FACE",FACE,{"disambiguationData":[OSD([subQ1,subQ18,subQ17,sQuery(id+"F0.wireOp",EDGE,"E53"),subQ16])],"isStart":false})]}),makeQuery(id+"F4.opExtrude","CAP_FACE",FACE,{"disambiguationData":[OSD([subQ1,subQ7,sQuery(id+"F0.wireOp",EDGE,"E20"),sQuery(id+"F0.wireOp",EDGE,"E22"),subQ11,subQ10,subQ13,subQ12,subQ4,subQ3,subQ9,subQ8,subQ6,subQ5])],"isStart":false})]}),makeQuery(id+"F5.opExtrude","CAP_FACE",FACE,{"disambiguationData":[OSD([subQ15,subQ14,subQ2,subQ7,subQ0,sQuery(id+"F0.wireOp",EDGE,"E29.0"),sQuery(id+"F0.wireOp",EDGE,"E30"),sQuery(id+"F0.wireOp",EDGE,"E31.0")])],"isStart":false})]}),makeQuery(id+"F6.opExtrude","CAP_FACE",FACE,{"disambiguationData":[OSD([subQ1,subQ13,subQ12,sQuery(id+"F0.wireOp",EDGE,"E41.0"),sQuery(id+"F0.wireOp",EDGE,"E42.0")])],"isStart":false}),makeQuery(id+"F6.opExtrude","CAP_FACE",FACE,{"disambiguationData":[OSD([subQ1,subQ11,subQ10,sQuery(id+"F0.wireOp",EDGE,"E43.0"),sQuery(id+"F0.wireOp",EDGE,"E44.0")])],"isStart":false}),makeQuery(id+"F6.opExtrude","CAP_FACE",FACE,{"disambiguationData":[OSD([subQ7,subQ9,subQ8,sQuery(id+"F0.wireOp",EDGE,"E39.0"),sQuery(id+"F0.wireOp",EDGE,"E40.0")])],"isStart":false}),makeQuery(id+"F6.opExtrude","CAP_FACE",FACE,{"disambiguationData":[OSD([subQ7,subQ6,subQ5,sQuery(id+"F0.wireOp",EDGE,"E37.0"),sQuery(id+"F0.wireOp",EDGE,"E38.0")])],"isStart":false})]}),makeQuery(id+"F7.opExtrude","CAP_FACE",FACE,{"disambiguationData":[OSD([subQ1,subQ4,subQ3,sQuery(id+"F0.wireOp",EDGE,"E48.0"),sQuery(id+"F0.wireOp",EDGE,"E49.0")])],"isStart":false})]}),makeQuery(id+"F8.opExtrude","CAP_FACE",FACE,{"disambiguationData":[OSD([subQ1,subQ2,sQuery(id+"F0.wireOp",EDGE,"E21"),sQuery(id+"F0.wireOp",EDGE,"E51.0")])],"isStart":false}),makeQuery(id+"F8.opExtrude","CAP_FACE",FACE,{"disambiguationData":[OSD([subQ1,subQ0,sQuery(id+"F0.wireOp",EDGE,"E19"),sQuery(id+"F0.wireOp",EDGE,"E50.0")])],"isStart":false})]});}
            extrude(context, id + "F9", {"entities" : qUnion([Q0]), "operationType" : NewBodyOperationType.ADD, "endBound" : BoundingType.UP_TO_SURFACE, "depth" : 12.7 * mm, "endBoundEntityFace" : qUnion([Q1]), "offsetDistance" : 25.4 * mm});
        }
        {
            var Q0;
            {var subQ0=sQuery(id+"F0.wireOp",EDGE,"E20");Q0=makeQuery(id+"F0.imprint","IMPRINT",FACE,{"disambiguationData":[TD([[makeQuery(id+"F0.imprint","IMPRINT",EDGE,{"derivedFrom":subQ0}),1.0]])]});}
            var Q1;
            {var subQ0=sQuery(id+"F0.wireOp",EDGE,"E22");var subQ1=sQuery(id+"F0.wireOp",EDGE,"E21");var subQ2=sQuery(id+"F0.wireOp",EDGE,"E16");var subQ3=sQuery(id+"F0.wireOp",EDGE,"E18");var subQ4=sQuery(id+"F0.wireOp",EDGE,"E0.bottom");var subQ5=sQuery(id+"F0.wireOp",EDGE,"E27.5");var subQ6=sQuery(id+"F0.wireOp",EDGE,"E27.4");var subQ7=sQuery(id+"F0.wireOp",EDGE,"E28.3");var subQ8=sQuery(id+"F0.wireOp",EDGE,"E28.2");var subQ9=sQuery(id+"F0.wireOp",EDGE,"E17");var subQ10=sQuery(id+"F0.wireOp",EDGE,"E28.1");var subQ11=sQuery(id+"F0.wireOp",EDGE,"E28.0");var subQ12=sQuery(id+"F0.wireOp",EDGE,"E27.1");var subQ13=sQuery(id+"F0.wireOp",EDGE,"E27.0");var subQ14=sQuery(id+"F0.wireOp",EDGE,"E27.3");var subQ15=sQuery(id+"F0.wireOp",EDGE,"E27.2");var subQ16=sQuery(id+"F0.wireOp",EDGE,"E2.bottom");var subQ17=sQuery(id+"F0.wireOp",EDGE,"E1.bottom");var subQ18=sQuery(id+"F0.wireOp",EDGE,"E72");var subQ19=sQuery(id+"F0.wireOp",EDGE,"E15");var subQ20=sQuery(id+"F0.wireOp",EDGE,"E1.left");var subQ21=sQuery(id+"F0.wireOp",EDGE,"E2.left");Q1=makeQuery(id+"F9.boolean.opBoolean","MERGE",FACE,{"derivedFrom":[makeQuery(id+"F8.boolean.opBoolean","MERGE",FACE,{"derivedFrom":[makeQuery(id+"F7.boolean.opBoolean","MERGE",FACE,{"derivedFrom":[makeQuery(id+"F6.boolean.opBoolean","MERGE",FACE,{"derivedFrom":[makeQuery(id+"F2.boolean.opBoolean","MERGE",FACE,{"derivedFrom":[makeQuery(id+"F1.opExtrude","CAP_FACE",FACE,{"disambiguationData":[OSD([subQ4,subQ16,subQ21,sQuery(id+"F0.wireOp",EDGE,"E2.right"),subQ18])],"isStart":false}),makeQuery(id+"F2.opExtrude","CAP_FACE",FACE,{"disambiguationData":[OSD([subQ4,subQ21,sQuery(id+"F0.wireOp",EDGE,"E54"),subQ18])],"isStart":false})]}),makeQuery(id+"F5.boolean.opBoolean","MERGE",FACE,{"derivedFrom":[makeQuery(id+"F4.boolean.opBoolean","MERGE",FACE,{"derivedFrom":[makeQuery(id+"F2.boolean.opBoolean","MERGE",FACE,{"derivedFrom":[makeQuery(id+"F1.opExtrude","CAP_FACE",FACE,{"disambiguationData":[OSD([subQ17,sQuery(id+"F0.wireOp",EDGE,"E1.top"),subQ20,sQuery(id+"F0.wireOp",EDGE,"E1.right"),subQ19])],"isStart":false}),makeQuery(id+"F2.opExtrude","CAP_FACE",FACE,{"disambiguationData":[OSD([subQ4,subQ20,subQ19,sQuery(id+"F0.wireOp",EDGE,"E53"),subQ18])],"isStart":false})]}),makeQuery(id+"F4.opExtrude","CAP_FACE",FACE,{"disambiguationData":[OSD([subQ4,subQ9,sQuery(id+"F0.wireOp",EDGE,"E20"),subQ0,subQ13,subQ12,subQ15,subQ14,subQ6,subQ5,subQ11,subQ10,subQ8,subQ7])],"isStart":false})]}),makeQuery(id+"F5.opExtrude","CAP_FACE",FACE,{"disambiguationData":[OSD([subQ17,subQ16,subQ2,subQ9,subQ3,sQuery(id+"F0.wireOp",EDGE,"E29.0"),sQuery(id+"F0.wireOp",EDGE,"E30"),sQuery(id+"F0.wireOp",EDGE,"E31.0")])],"isStart":false})]}),makeQuery(id+"F6.opExtrude","CAP_FACE",FACE,{"disambiguationData":[OSD([subQ4,subQ15,subQ14,sQuery(id+"F0.wireOp",EDGE,"E41.0"),sQuery(id+"F0.wireOp",EDGE,"E42.0")])],"isStart":false}),makeQuery(id+"F6.opExtrude","CAP_FACE",FACE,{"disambiguationData":[OSD([subQ4,subQ13,subQ12,sQuery(id+"F0.wireOp",EDGE,"E43.0"),sQuery(id+"F0.wireOp",EDGE,"E44.0")])],"isStart":false}),makeQuery(id+"F6.opExtrude","CAP_FACE",FACE,{"disambiguationData":[OSD([subQ9,subQ11,subQ10,sQuery(id+"F0.wireOp",EDGE,"E39.0"),sQuery(id+"F0.wireOp",EDGE,"E40.0")])],"isStart":false}),makeQuery(id+"F6.opExtrude","CAP_FACE",FACE,{"disambiguationData":[OSD([subQ9,subQ8,subQ7,sQuery(id+"F0.wireOp",EDGE,"E37.0"),sQuery(id+"F0.wireOp",EDGE,"E38.0")])],"isStart":false})]}),makeQuery(id+"F7.opExtrude","CAP_FACE",FACE,{"disambiguationData":[OSD([subQ4,subQ6,subQ5,sQuery(id+"F0.wireOp",EDGE,"E48.0"),sQuery(id+"F0.wireOp",EDGE,"E49.0")])],"isStart":false})]}),makeQuery(id+"F8.opExtrude","CAP_FACE",FACE,{"disambiguationData":[OSD([subQ4,subQ2,subQ1,sQuery(id+"F0.wireOp",EDGE,"E51.0")])],"isStart":false}),makeQuery(id+"F8.opExtrude","CAP_FACE",FACE,{"disambiguationData":[OSD([subQ4,subQ3,sQuery(id+"F0.wireOp",EDGE,"E19"),sQuery(id+"F0.wireOp",EDGE,"E50.0")])],"isStart":false})]}),makeQuery(id+"F9.opExtrude","CAP_FACE",FACE,{"disambiguationData":[OSD([subQ2,subQ1,subQ0,sQuery(id+"F0.wireOp",EDGE,"E52.0")])],"isStart":false})]});}
            extrude(context, id + "F10", {"entities" : qUnion([Q0]), "operationType" : NewBodyOperationType.ADD, "endBound" : BoundingType.UP_TO_SURFACE, "depth" : 25.4 * mm, "endBoundEntityFace" : qUnion([Q1]), "offsetDistance" : 25.4 * mm});
        }
        {
            var Q0;
            {var subQ24=sQuery(id+"F0.wireOp",EDGE,"E59.0");Q0=makeQuery(id+"F0.imprint","IMPRINT",FACE,{"disambiguationData":[TD([[makeQuery(id+"F0.imprint","IMPRINT",EDGE,{"derivedFrom":subQ24}),1.0]])]});}
            var Q1;
            {var subQ0=sQuery(id+"F0.wireOp",EDGE,"E20");var subQ1=sQuery(id+"F0.wireOp",EDGE,"E19");var subQ2=sQuery(id+"F0.wireOp",EDGE,"E18");var subQ3=sQuery(id+"F0.wireOp",EDGE,"E22");var subQ4=sQuery(id+"F0.wireOp",EDGE,"E21");var subQ5=sQuery(id+"F0.wireOp",EDGE,"E16");var subQ6=sQuery(id+"F0.wireOp",EDGE,"E0.bottom");var subQ7=sQuery(id+"F0.wireOp",EDGE,"E27.5");var subQ8=sQuery(id+"F0.wireOp",EDGE,"E27.4");var subQ9=sQuery(id+"F0.wireOp",EDGE,"E28.3");var subQ10=sQuery(id+"F0.wireOp",EDGE,"E28.2");var subQ11=sQuery(id+"F0.wireOp",EDGE,"E17");var subQ12=sQuery(id+"F0.wireOp",EDGE,"E28.1");var subQ13=sQuery(id+"F0.wireOp",EDGE,"E28.0");var subQ14=sQuery(id+"F0.wireOp",EDGE,"E27.1");var subQ15=sQuery(id+"F0.wireOp",EDGE,"E27.0");var subQ16=sQuery(id+"F0.wireOp",EDGE,"E27.3");var subQ17=sQuery(id+"F0.wireOp",EDGE,"E27.2");var subQ18=sQuery(id+"F0.wireOp",EDGE,"E2.bottom");var subQ19=sQuery(id+"F0.wireOp",EDGE,"E1.bottom");var subQ20=sQuery(id+"F0.wireOp",EDGE,"E72");var subQ21=sQuery(id+"F0.wireOp",EDGE,"E15");var subQ22=sQuery(id+"F0.wireOp",EDGE,"E1.left");var subQ23=sQuery(id+"F0.wireOp",EDGE,"E2.left");Q1=makeQuery(id+"F10.boolean.opBoolean","MERGE",FACE,{"derivedFrom":[makeQuery(id+"F9.boolean.opBoolean","MERGE",FACE,{"derivedFrom":[makeQuery(id+"F8.boolean.opBoolean","MERGE",FACE,{"derivedFrom":[makeQuery(id+"F7.boolean.opBoolean","MERGE",FACE,{"derivedFrom":[makeQuery(id+"F6.boolean.opBoolean","MERGE",FACE,{"derivedFrom":[makeQuery(id+"F2.boolean.opBoolean","MERGE",FACE,{"derivedFrom":[makeQuery(id+"F1.opExtrude","CAP_FACE",FACE,{"disambiguationData":[OSD([subQ6,subQ18,subQ23,sQuery(id+"F0.wireOp",EDGE,"E2.right"),subQ20])],"isStart":false}),makeQuery(id+"F2.opExtrude","CAP_FACE",FACE,{"disambiguationData":[OSD([subQ6,subQ23,sQuery(id+"F0.wireOp",EDGE,"E54"),subQ20])],"isStart":false})]}),makeQuery(id+"F5.boolean.opBoolean","MERGE",FACE,{"derivedFrom":[makeQuery(id+"F4.boolean.opBoolean","MERGE",FACE,{"derivedFrom":[makeQuery(id+"F2.boolean.opBoolean","MERGE",FACE,{"derivedFrom":[makeQuery(id+"F1.opExtrude","CAP_FACE",FACE,{"disambiguationData":[OSD([subQ19,sQuery(id+"F0.wireOp",EDGE,"E1.top"),subQ22,sQuery(id+"F0.wireOp",EDGE,"E1.right"),subQ21])],"isStart":false}),makeQuery(id+"F2.opExtrude","CAP_FACE",FACE,{"disambiguationData":[OSD([subQ6,subQ22,subQ21,sQuery(id+"F0.wireOp",EDGE,"E53"),subQ20])],"isStart":false})]}),makeQuery(id+"F4.opExtrude","CAP_FACE",FACE,{"disambiguationData":[OSD([subQ6,subQ11,subQ0,subQ3,subQ15,subQ14,subQ17,subQ16,subQ8,subQ7,subQ13,subQ12,subQ10,subQ9])],"isStart":false})]}),makeQuery(id+"F5.opExtrude","CAP_FACE",FACE,{"disambiguationData":[OSD([subQ19,subQ18,subQ5,subQ11,subQ2,sQuery(id+"F0.wireOp",EDGE,"E29.0"),sQuery(id+"F0.wireOp",EDGE,"E30"),sQuery(id+"F0.wireOp",EDGE,"E31.0")])],"isStart":false})]}),makeQuery(id+"F6.opExtrude","CAP_FACE",FACE,{"disambiguationData":[OSD([subQ6,subQ17,subQ16,sQuery(id+"F0.wireOp",EDGE,"E41.0"),sQuery(id+"F0.wireOp",EDGE,"E42.0")])],"isStart":false}),makeQuery(id+"F6.opExtrude","CAP_FACE",FACE,{"disambiguationData":[OSD([subQ6,subQ15,subQ14,sQuery(id+"F0.wireOp",EDGE,"E43.0"),sQuery(id+"F0.wireOp",EDGE,"E44.0")])],"isStart":false}),makeQuery(id+"F6.opExtrude","CAP_FACE",FACE,{"disambiguationData":[OSD([subQ11,subQ13,subQ12,sQuery(id+"F0.wireOp",EDGE,"E39.0"),sQuery(id+"F0.wireOp",EDGE,"E40.0")])],"isStart":false}),makeQuery(id+"F6.opExtrude","CAP_FACE",FACE,{"disambiguationData":[OSD([subQ11,subQ10,subQ9,sQuery(id+"F0.wireOp",EDGE,"E37.0"),sQuery(id+"F0.wireOp",EDGE,"E38.0")])],"isStart":false})]}),makeQuery(id+"F7.opExtrude","CAP_FACE",FACE,{"disambiguationData":[OSD([subQ6,subQ8,subQ7,sQuery(id+"F0.wireOp",EDGE,"E48.0"),sQuery(id+"F0.wireOp",EDGE,"E49.0")])],"isStart":false})]}),makeQuery(id+"F8.opExtrude","CAP_FACE",FACE,{"disambiguationData":[OSD([subQ6,subQ5,subQ4,sQuery(id+"F0.wireOp",EDGE,"E51.0")])],"isStart":false}),makeQuery(id+"F8.opExtrude","CAP_FACE",FACE,{"disambiguationData":[OSD([subQ6,subQ2,subQ1,sQuery(id+"F0.wireOp",EDGE,"E50.0")])],"isStart":false})]}),makeQuery(id+"F9.opExtrude","CAP_FACE",FACE,{"disambiguationData":[OSD([subQ5,subQ4,subQ3,sQuery(id+"F0.wireOp",EDGE,"E52.0")])],"isStart":false})]}),makeQuery(id+"F10.opExtrude","CAP_FACE",FACE,{"disambiguationData":[OSD([subQ2,subQ1,subQ0,sQuery(id+"F0.wireOp",EDGE,"E55.0")])],"isStart":false})]});}
            extrude(context, id + "F11", {"entities" : qUnion([Q0]), "operationType" : NewBodyOperationType.ADD, "endBound" : BoundingType.UP_TO_SURFACE, "depth" : 25.4 * mm, "endBoundEntityFace" : qUnion([Q1]), "offsetDistance" : 25.4 * mm});
        }
        {
            var Q0;
            {var subQ28=sQuery(id+"F0.wireOp",EDGE,"E29.0");Q0=makeQuery(id+"F0.imprint","IMPRINT",FACE,{"disambiguationData":[TD([[makeQuery(id+"F0.imprint","IMPRINT",EDGE,{"derivedFrom":subQ28}),1.0]])]});}
            var sketch = newSketch(context, id + "F12", { "sketchPlane" : qUnion([Q0])});
            skLineSegment(sketch, "E73.bottom", {"start": v(43.97, 27.89) * mm, "end": v(42.1, 27.89) * mm});
            skLineSegment(sketch, "E73.top", {"start": v(43.97, 24.3) * mm, "end": v(42.1, 24.3) * mm});
            skLineSegment(sketch, "E73.left", {"start": v(43.97, 27.89) * mm, "end": v(43.97, 24.3) * mm});
            skLineSegment(sketch, "E73.right", {"start": v(42.1, 27.89) * mm, "end": v(42.1, 24.3) * mm});
            skLineSegment(sketch, "E74.bottom", {"start": v(23.77, 24.3) * mm, "end": v(21.23, 24.3) * mm});
            skLineSegment(sketch, "E74.top", {"start": v(23.77, 27.89) * mm, "end": v(21.23, 27.89) * mm});
            skLineSegment(sketch, "E74.left", {"start": v(23.77, 24.3) * mm, "end": v(23.77, 27.89) * mm});
            skLineSegment(sketch, "E74.right", {"start": v(21.23, 24.3) * mm, "end": v(21.23, 27.89) * mm});
            skLineSegment(sketch, "E75.bottom", {"start": v(1.93, 27.89) * mm, "end": v(-1.93, 27.89) * mm});
            skLineSegment(sketch, "E75.top", {"start": v(1.93, 24.3) * mm, "end": v(-1.93, 24.3) * mm});
            skLineSegment(sketch, "E75.left", {"start": v(1.93, 27.89) * mm, "end": v(1.93, 24.3) * mm});
            skLineSegment(sketch, "E75.right", {"start": v(-1.93, 27.89) * mm, "end": v(-1.93, 24.3) * mm});
            skLineSegment(sketch, "E76.bottom", {"start": v(-21.23, 27.89) * mm, "end": v(-23.77, 27.89) * mm});
            skLineSegment(sketch, "E76.top", {"start": v(-21.23, 24.3) * mm, "end": v(-23.77, 24.3) * mm});
            skLineSegment(sketch, "E76.left", {"start": v(-21.23, 27.89) * mm, "end": v(-21.23, 24.3) * mm});
            skLineSegment(sketch, "E76.right", {"start": v(-23.77, 27.89) * mm, "end": v(-23.77, 24.3) * mm});
            skLineSegment(sketch, "E77.bottom", {"start": v(-42.1, 27.89) * mm, "end": v(-43.97, 27.89) * mm});
            skLineSegment(sketch, "E77.top", {"start": v(-42.1, 24.3) * mm, "end": v(-43.97, 24.3) * mm});
            skLineSegment(sketch, "E77.left", {"start": v(-42.1, 27.89) * mm, "end": v(-42.1, 24.3) * mm});
            skLineSegment(sketch, "E77.right", {"start": v(-43.97, 27.89) * mm, "end": v(-43.97, 24.3) * mm});
            skSolve(sketch);
        }
        {
            var Q0;
            {var subQ0=sQuery(id+"F0.wireOp",EDGE,"E0.bottom");var subQ2=makeQuery(id+"F0.imprint","INTERSECT",VERTEX,{"derivedFrom":[subQ0,sQuery(id+"F0.wireOp",EDGE,"E41.0")]});var subQ3=makeQuery(id+"F0.imprint","INTERSECT",VERTEX,{"derivedFrom":[subQ0,sQuery(id+"F0.wireOp",EDGE,"E42.0")]});var subQ5=makeQuery(id+"F0.imprint","INTERSECT",VERTEX,{"derivedFrom":[subQ0,sQuery(id+"F0.wireOp",EDGE,"E27.2")]});var subQ7=makeQuery(id+"F0.imprint","INTERSECT",VERTEX,{"derivedFrom":[subQ0,sQuery(id+"F0.wireOp",EDGE,"E27.3")]});var subQ8=makeQuery(id+"F0.imprint","INTERSECT",VERTEX,{"derivedFrom":[subQ0,sQuery(id+"F0.wireOp",EDGE,"E27.4")]});var subQ9=makeQuery(id+"F0.imprint","INTERSECT",VERTEX,{"derivedFrom":[subQ0,sQuery(id+"F0.wireOp",EDGE,"E50.0")]});var subQ10=sQuery(id+"F0.wireOp",EDGE,"E1.bottom");var subQ11=makeQuery(id+"F0.imprint","INTERSECT",VERTEX,{"derivedFrom":[subQ0,sQuery(id+"F0.wireOp",EDGE,"E49.0")]});var subQ12=makeQuery(id+"F0.imprint","INTERSECT",VERTEX,{"derivedFrom":[subQ0,sQuery(id+"F0.wireOp",EDGE,"E54")]});var subQ14=makeQuery(id+"F0.imprint","INTERSECT",VERTEX,{"derivedFrom":[subQ0,sQuery(id+"F0.wireOp",EDGE,"E43.0")]});var subQ15=makeQuery(id+"F0.imprint","INTERSECT",VERTEX,{"derivedFrom":[subQ0,sQuery(id+"F0.wireOp",EDGE,"E44.0")]});var subQ17=makeQuery(id+"F0.imprint","INTERSECT",VERTEX,{"derivedFrom":[subQ0,sQuery(id+"F0.wireOp",EDGE,"E27.0")]});var subQ18=makeQuery(id+"F0.imprint","INTERSECT",VERTEX,{"derivedFrom":[subQ0,sQuery(id+"F0.wireOp",EDGE,"E27.1")]});var subQ20=makeQuery(id+"F0.imprint","INTERSECT",VERTEX,{"derivedFrom":[subQ0,sQuery(id+"F0.wireOp",EDGE,"E27.5")]});var subQ21=makeQuery(id+"F0.imprint","INTERSECT",VERTEX,{"derivedFrom":[subQ0,sQuery(id+"F0.wireOp",EDGE,"E51.0")]});Q0=qUnion([makeQuery(id+"F3.boolean.opBoolean","MERGE",FACE,{"derivedFrom":[makeQuery(id+"F2.boolean.opBoolean","MERGE",FACE,{"derivedFrom":[makeQuery(id+"F1.opExtrude","SWEPT_FACE",FACE,{"disambiguationData":[OSD([subQ0,sQuery(id+"F0.wireOp",EDGE,"E2.bottom")])]}),makeQuery(id+"F2.opExtrude","SWEPT_FACE",FACE,{"disambiguationData":[OSD([subQ0]),TDD([makeQuery(id+"F0.imprint","IMPRINT",EDGE,{"disambiguationData":[TD([[subQ18,-1.0]])],"derivedFrom":subQ0}),makeQuery(id+"F0.imprint","IMPRINT",EDGE,{"disambiguationData":[TD([[subQ12,-1.0]])],"derivedFrom":subQ0}),makeQuery(id+"F0.imprint","IMPRINT",EDGE,{"disambiguationData":[TD([[subQ15,-1.0]])],"derivedFrom":subQ0}),makeQuery(id+"F0.imprint","IMPRINT",EDGE,{"disambiguationData":[TD([[makeQuery(id+"F0.imprint","INTERSECT",VERTEX,{"derivedFrom":[subQ0,sQuery(id+"F0.wireOp",EDGE,"E2.left")]}),1.0]])],"derivedFrom":subQ0}),makeQuery(id+"F0.imprint","IMPRINT",EDGE,{"disambiguationData":[TD([[subQ21,1.0]])],"derivedFrom":subQ0}),makeQuery(id+"F0.imprint","IMPRINT",EDGE,{"disambiguationData":[TD([[subQ20,-1.0]])],"derivedFrom":subQ0}),makeQuery(id+"F0.imprint","IMPRINT",EDGE,{"disambiguationData":[TD([[subQ18,1.0]])],"derivedFrom":subQ0}),makeQuery(id+"F0.imprint","IMPRINT",EDGE,{"disambiguationData":[TD([[subQ17,-1.0]])],"derivedFrom":subQ0}),makeQuery(id+"F0.imprint","IMPRINT",EDGE,{"disambiguationData":[TD([[subQ15,1.0]])],"derivedFrom":subQ0}),makeQuery(id+"F0.imprint","IMPRINT",EDGE,{"disambiguationData":[TD([[subQ14,-1.0]])],"derivedFrom":subQ0})])]})]}),makeQuery(id+"F3.opExtrude","SWEPT_FACE",FACE,{"disambiguationData":[OSD([subQ0]),TDD([makeQuery(id+"F0.imprint","IMPRINT",EDGE,{"disambiguationData":[TD([[subQ12,1.0]])],"derivedFrom":subQ0}),makeQuery(id+"F0.imprint","IMPRINT",EDGE,{"disambiguationData":[TD([[subQ11,1.0]])],"derivedFrom":subQ0})])]})]}),makeQuery(id+"F2.boolean.opBoolean","MERGE",FACE,{"derivedFrom":[makeQuery(id+"F1.opExtrude","SWEPT_FACE",FACE,{"disambiguationData":[OSD([subQ10])]}),makeQuery(id+"F2.opExtrude","SWEPT_FACE",FACE,{"disambiguationData":[OSD([subQ0]),TDD([makeQuery(id+"F0.imprint","IMPRINT",EDGE,{"disambiguationData":[TD([[subQ2,-1.0]])],"derivedFrom":subQ0}),makeQuery(id+"F0.imprint","IMPRINT",EDGE,{"disambiguationData":[TD([[subQ8,-1.0]])],"derivedFrom":subQ0}),makeQuery(id+"F0.imprint","IMPRINT",EDGE,{"disambiguationData":[TD([[subQ5,-1.0]])],"derivedFrom":subQ0}),makeQuery(id+"F0.imprint","IMPRINT",EDGE,{"disambiguationData":[TD([[subQ9,1.0]])],"derivedFrom":subQ0}),makeQuery(id+"F0.imprint","IMPRINT",EDGE,{"disambiguationData":[TD([[subQ9,-1.0]])],"derivedFrom":subQ0}),makeQuery(id+"F0.imprint","IMPRINT",EDGE,{"disambiguationData":[TD([[subQ8,1.0]])],"derivedFrom":subQ0}),makeQuery(id+"F0.imprint","IMPRINT",EDGE,{"disambiguationData":[TD([[subQ7,-1.0]])],"derivedFrom":subQ0}),makeQuery(id+"F0.imprint","IMPRINT",EDGE,{"disambiguationData":[TD([[subQ5,1.0]])],"derivedFrom":subQ0}),makeQuery(id+"F0.imprint","IMPRINT",EDGE,{"disambiguationData":[TD([[subQ3,-1.0]])],"derivedFrom":subQ0}),makeQuery(id+"F0.imprint","IMPRINT",EDGE,{"disambiguationData":[TD([[subQ2,1.0]])],"derivedFrom":subQ0})])]})]})]);}
            var sketch = newSketch(context, id + "F13", { "sketchPlane" : qUnion([Q0])});
            skLineSegment(sketch, "E78.bottom", {"start": v(-7.62, 13.97) * mm, "end": v(7.62, 13.97) * mm});
            skLineSegment(sketch, "E78.top", {"start": v(-7.62, -1.27) * mm, "end": v(7.62, -1.27) * mm});
            skLineSegment(sketch, "E78.left", {"start": v(-7.62, 13.97) * mm, "end": v(-7.62, -1.27) * mm});
            skLineSegment(sketch, "E78.right", {"start": v(7.62, 13.97) * mm, "end": v(7.62, -1.27) * mm});
            skPoint(sketch, "E79", {"position": v(7.62, 6.35) * mm});
            skSolve(sketch);
        }
        {
            var Q0;
            {var subQ0=sQuery(id+"F0.wireOp",EDGE,"E2.left");var subQ1=sQuery(id+"F0.wireOp",EDGE,"E2.bottom");var subQ12=sQuery(id+"F0.wireOp",EDGE,"E54");var subQ15=sQuery(id+"F0.wireOp",EDGE,"E2.top");Q0=makeQuery(id+"FNRWj5r8XRpMM9b_2.opPattern","COPY",FACE,{"derivedFrom":makeQuery(id+"F3.boolean.opBoolean","SPLIT",FACE,{"disambiguationData":[TD([makeQuery(id+"F1.opExtrude","CAP_FACE",FACE,{"disambiguationData":[OSD([subQ1,subQ15,subQ0,sQuery(id+"F0.wireOp",EDGE,"E2.right")])],"isStart":false})])],"derivedFrom":makeQuery(id+"F2.opExtrude","SWEPT_FACE",FACE,{"disambiguationData":[OSD([subQ12])]})}),"instanceName":"1"});}
            var Q1;
            {var subQ1=sQuery(id+"F0.wireOp",EDGE,"E0.bottom");var subQ12=sQuery(id+"F0.wireOp",EDGE,"E2.left");var subQ13=sQuery(id+"F0.wireOp",EDGE,"E54");var subQ15=sQuery(id+"F0.wireOp",EDGE,"E72");Q1=makeQuery(id+"F3.boolean.opBoolean","SPLIT",FACE,{"disambiguationData":[TD([makeQuery(id+"F2.opExtrude","CAP_FACE",FACE,{"disambiguationData":[OSD([subQ1,subQ12,subQ13,subQ15])],"isStart":false})])],"derivedFrom":makeQuery(id+"F2.opExtrude","SWEPT_FACE",FACE,{"disambiguationData":[OSD([subQ13])]})});}
            extrude(context, id + "F14", {"entities" : qUnion([Q0, Q1]), "operationType" : NewBodyOperationType.ADD, "endBound" : BoundingType.UP_TO_NEXT, "depth" : 25.4 * mm, "offsetDistance" : 25.4 * mm});
        }
        {
            var Q0;
            Q0=makeQuery(id+"F3.opExtrude","SWEPT_FACE",FACE,{"disambiguationData":[OSD([sQuery(id+"F0.wireOp",EDGE,"E11")])]});
            extrude(context, id + "F15", {"entities" : qUnion([Q0]), "operationType" : NewBodyOperationType.ADD, "endBound" : BoundingType.UP_TO_NEXT, "depth" : 25.4 * mm, "offsetDistance" : 25.4 * mm});
        }
        {
            var Q0;
            {var subQ0=sQuery(id+"F0.wireOp",EDGE,"E61");Q0=makeQuery(id+"F0.imprint","IMPRINT",FACE,{"disambiguationData":[TD([[makeQuery(id+"F0.imprint","IMPRINT",EDGE,{"derivedFrom":subQ0}),-1.0]])]});}
            var Q1;
            {var subQ2=sQuery(id+"F0.wireOp",EDGE,"E60");Q1=makeQuery(id+"F0.imprint","IMPRINT",FACE,{"disambiguationData":[TD([[makeQuery(id+"F0.imprint","IMPRINT",EDGE,{"derivedFrom":subQ2}),-1.0]])]});}
            var Q2;
            {var subQ2=sQuery(id+"F0.wireOp",EDGE,"E63");Q2=makeQuery(id+"F0.imprint","IMPRINT",FACE,{"disambiguationData":[TD([[makeQuery(id+"F0.imprint","IMPRINT",EDGE,{"derivedFrom":subQ2}),-1.0]])]});}
            var Q3;
            {var subQ3=sQuery(id+"F0.wireOp",EDGE,"E64.0");var subQ5=sQuery(id+"F0.wireOp",EDGE,"E72");var subQ7=makeQuery(id+"F0.imprint","INTERSECT",VERTEX,{"derivedFrom":[subQ3,subQ5]});Q3=makeQuery(id+"F0.imprint","IMPRINT",FACE,{"disambiguationData":[TD([[makeQuery(id+"F0.imprint","IMPRINT",EDGE,{"disambiguationData":[TD([[subQ7,-1.0]])],"derivedFrom":subQ3}),1.0]])]});}
            var Q4;
            {var subQ0=sQuery(id+"F0.wireOp",EDGE,"E54");var subQ1=sQuery(id+"F0.wireOp",EDGE,"E72");var subQ2=sQuery(id+"F0.wireOp",EDGE,"E20");var subQ3=sQuery(id+"F0.wireOp",EDGE,"E19");var subQ4=sQuery(id+"F0.wireOp",EDGE,"E18");var subQ5=sQuery(id+"F0.wireOp",EDGE,"E22");var subQ6=sQuery(id+"F0.wireOp",EDGE,"E21");var subQ7=sQuery(id+"F0.wireOp",EDGE,"E16");var subQ8=sQuery(id+"F0.wireOp",EDGE,"E0.bottom");var subQ9=sQuery(id+"F0.wireOp",EDGE,"E27.5");var subQ10=sQuery(id+"F0.wireOp",EDGE,"E27.4");var subQ11=sQuery(id+"F0.wireOp",EDGE,"E28.3");var subQ12=sQuery(id+"F0.wireOp",EDGE,"E28.2");var subQ13=sQuery(id+"F0.wireOp",EDGE,"E17");var subQ14=sQuery(id+"F0.wireOp",EDGE,"E28.1");var subQ15=sQuery(id+"F0.wireOp",EDGE,"E28.0");var subQ16=sQuery(id+"F0.wireOp",EDGE,"E27.1");var subQ17=sQuery(id+"F0.wireOp",EDGE,"E27.0");var subQ18=sQuery(id+"F0.wireOp",EDGE,"E27.3");var subQ19=sQuery(id+"F0.wireOp",EDGE,"E27.2");var subQ20=sQuery(id+"F0.wireOp",EDGE,"E2.bottom");var subQ21=sQuery(id+"F0.wireOp",EDGE,"E1.bottom");var subQ22=sQuery(id+"F0.wireOp",EDGE,"E15");var subQ23=sQuery(id+"F0.wireOp",EDGE,"E1.left");var subQ24=sQuery(id+"F0.wireOp",EDGE,"E2.left");Q4=makeQuery(id+"F14.boolean.opBoolean","MERGE",FACE,{"derivedFrom":[makeQuery(id+"F11.boolean.opBoolean","MERGE",FACE,{"derivedFrom":[makeQuery(id+"F10.boolean.opBoolean","MERGE",FACE,{"derivedFrom":[makeQuery(id+"F9.boolean.opBoolean","MERGE",FACE,{"derivedFrom":[makeQuery(id+"F8.boolean.opBoolean","MERGE",FACE,{"derivedFrom":[makeQuery(id+"F7.boolean.opBoolean","MERGE",FACE,{"derivedFrom":[makeQuery(id+"F6.boolean.opBoolean","MERGE",FACE,{"derivedFrom":[makeQuery(id+"F2.boolean.opBoolean","MERGE",FACE,{"derivedFrom":[makeQuery(id+"F1.opExtrude","CAP_FACE",FACE,{"disambiguationData":[OSD([subQ8,subQ20,subQ24,sQuery(id+"F0.wireOp",EDGE,"E2.right"),subQ1])],"isStart":false}),makeQuery(id+"F2.opExtrude","CAP_FACE",FACE,{"disambiguationData":[OSD([subQ8,subQ24,subQ0,subQ1])],"isStart":false})]}),makeQuery(id+"F5.boolean.opBoolean","MERGE",FACE,{"derivedFrom":[makeQuery(id+"F4.boolean.opBoolean","MERGE",FACE,{"derivedFrom":[makeQuery(id+"F2.boolean.opBoolean","MERGE",FACE,{"derivedFrom":[makeQuery(id+"F1.opExtrude","CAP_FACE",FACE,{"disambiguationData":[OSD([subQ21,sQuery(id+"F0.wireOp",EDGE,"E1.top"),subQ23,sQuery(id+"F0.wireOp",EDGE,"E1.right"),subQ22])],"isStart":false}),makeQuery(id+"F2.opExtrude","CAP_FACE",FACE,{"disambiguationData":[OSD([subQ8,subQ23,subQ22,sQuery(id+"F0.wireOp",EDGE,"E53"),subQ1])],"isStart":false})]}),makeQuery(id+"F4.opExtrude","CAP_FACE",FACE,{"disambiguationData":[OSD([subQ8,subQ13,subQ2,subQ5,subQ17,subQ16,subQ19,subQ18,subQ10,subQ9,subQ15,subQ14,subQ12,subQ11])],"isStart":false})]}),makeQuery(id+"F5.opExtrude","CAP_FACE",FACE,{"disambiguationData":[OSD([subQ21,subQ20,subQ7,subQ13,subQ4,sQuery(id+"F0.wireOp",EDGE,"E29.0"),sQuery(id+"F0.wireOp",EDGE,"E30"),sQuery(id+"F0.wireOp",EDGE,"E31.0")])],"isStart":false})]}),makeQuery(id+"F6.opExtrude","CAP_FACE",FACE,{"disambiguationData":[OSD([subQ8,subQ19,subQ18,sQuery(id+"F0.wireOp",EDGE,"E41.0"),sQuery(id+"F0.wireOp",EDGE,"E42.0")])],"isStart":false}),makeQuery(id+"F6.opExtrude","CAP_FACE",FACE,{"disambiguationData":[OSD([subQ8,subQ17,subQ16,sQuery(id+"F0.wireOp",EDGE,"E43.0"),sQuery(id+"F0.wireOp",EDGE,"E44.0")])],"isStart":false}),makeQuery(id+"F6.opExtrude","CAP_FACE",FACE,{"disambiguationData":[OSD([subQ13,subQ15,subQ14,sQuery(id+"F0.wireOp",EDGE,"E39.0"),sQuery(id+"F0.wireOp",EDGE,"E40.0")])],"isStart":false}),makeQuery(id+"F6.opExtrude","CAP_FACE",FACE,{"disambiguationData":[OSD([subQ13,subQ12,subQ11,sQuery(id+"F0.wireOp",EDGE,"E37.0"),sQuery(id+"F0.wireOp",EDGE,"E38.0")])],"isStart":false})]}),makeQuery(id+"F7.opExtrude","CAP_FACE",FACE,{"disambiguationData":[OSD([subQ8,subQ10,subQ9,sQuery(id+"F0.wireOp",EDGE,"E48.0"),sQuery(id+"F0.wireOp",EDGE,"E49.0")])],"isStart":false})]}),makeQuery(id+"F8.opExtrude","CAP_FACE",FACE,{"disambiguationData":[OSD([subQ8,subQ7,subQ6,sQuery(id+"F0.wireOp",EDGE,"E51.0")])],"isStart":false}),makeQuery(id+"F8.opExtrude","CAP_FACE",FACE,{"disambiguationData":[OSD([subQ8,subQ4,subQ3,sQuery(id+"F0.wireOp",EDGE,"E50.0")])],"isStart":false})]}),makeQuery(id+"F9.opExtrude","CAP_FACE",FACE,{"disambiguationData":[OSD([subQ7,subQ6,subQ5,sQuery(id+"F0.wireOp",EDGE,"E52.0")])],"isStart":false})]}),makeQuery(id+"F10.opExtrude","CAP_FACE",FACE,{"disambiguationData":[OSD([subQ4,subQ3,subQ2,sQuery(id+"F0.wireOp",EDGE,"E55.0")])],"isStart":false})]}),makeQuery(id+"F11.opExtrude","CAP_FACE",FACE,{"disambiguationData":[OSD([sQuery(id+"F0.wireOp",EDGE,"E56"),sQuery(id+"F0.wireOp",EDGE,"E57"),sQuery(id+"F0.wireOp",EDGE,"E58"),sQuery(id+"F0.wireOp",EDGE,"E59.0"),sQuery(id+"F0.wireOp",EDGE,"E59.1"),sQuery(id+"F0.wireOp",EDGE,"E59.2"),subQ1])],"isStart":false})]}),makeQuery(id+"F14.opExtrude","SWEPT_FACE",FACE,{"disambiguationData":[OSD([subQ0]),TDD([makeQuery(id+"F2.opExtrude","CAP_EDGE",EDGE,{"disambiguationData":[OSD([subQ0])],"isStart":false})])]})]});}
            extrude(context, id + "F16", {"entities" : qUnion([Q0, Q1, Q2, Q3]), "operationType" : NewBodyOperationType.ADD, "endBound" : BoundingType.UP_TO_SURFACE, "depth" : 25.4 * mm, "endBoundEntityFace" : qUnion([Q4]), "offsetDistance" : 25.4 * mm});
        }
        {
            var Q0;
            {var subQ2=sQuery(id+"F0.wireOp",EDGE,"E70");Q0=makeQuery(id+"F0.imprint","IMPRINT",FACE,{"disambiguationData":[TD([[makeQuery(id+"F0.imprint","IMPRINT",EDGE,{"derivedFrom":subQ2}),1.0]])]});}
            var Q1;
            {var subQ0=sQuery(id+"F0.wireOp",EDGE,"E72");var subQ1=sQuery(id+"F0.wireOp",EDGE,"E58");var subQ2=sQuery(id+"F0.wireOp",EDGE,"E57");var subQ3=sQuery(id+"F0.wireOp",EDGE,"E56");var subQ4=sQuery(id+"F0.wireOp",EDGE,"E54");var subQ5=sQuery(id+"F0.wireOp",EDGE,"E20");var subQ6=sQuery(id+"F0.wireOp",EDGE,"E19");var subQ7=sQuery(id+"F0.wireOp",EDGE,"E18");var subQ8=sQuery(id+"F0.wireOp",EDGE,"E22");var subQ9=sQuery(id+"F0.wireOp",EDGE,"E21");var subQ10=sQuery(id+"F0.wireOp",EDGE,"E16");var subQ11=sQuery(id+"F0.wireOp",EDGE,"E0.bottom");var subQ12=sQuery(id+"F0.wireOp",EDGE,"E27.5");var subQ13=sQuery(id+"F0.wireOp",EDGE,"E27.4");var subQ14=sQuery(id+"F0.wireOp",EDGE,"E28.3");var subQ15=sQuery(id+"F0.wireOp",EDGE,"E28.2");var subQ16=sQuery(id+"F0.wireOp",EDGE,"E17");var subQ17=sQuery(id+"F0.wireOp",EDGE,"E28.1");var subQ18=sQuery(id+"F0.wireOp",EDGE,"E28.0");var subQ19=sQuery(id+"F0.wireOp",EDGE,"E27.1");var subQ20=sQuery(id+"F0.wireOp",EDGE,"E27.0");var subQ21=sQuery(id+"F0.wireOp",EDGE,"E27.3");var subQ22=sQuery(id+"F0.wireOp",EDGE,"E27.2");var subQ23=sQuery(id+"F0.wireOp",EDGE,"E2.bottom");var subQ24=sQuery(id+"F0.wireOp",EDGE,"E1.bottom");var subQ25=sQuery(id+"F0.wireOp",EDGE,"E15");var subQ26=sQuery(id+"F0.wireOp",EDGE,"E1.left");var subQ27=sQuery(id+"F0.wireOp",EDGE,"E2.left");Q1=makeQuery(id+"F16.boolean.opBoolean","MERGE",FACE,{"derivedFrom":[makeQuery(id+"F14.boolean.opBoolean","MERGE",FACE,{"derivedFrom":[makeQuery(id+"F11.boolean.opBoolean","MERGE",FACE,{"derivedFrom":[makeQuery(id+"F10.boolean.opBoolean","MERGE",FACE,{"derivedFrom":[makeQuery(id+"F9.boolean.opBoolean","MERGE",FACE,{"derivedFrom":[makeQuery(id+"F8.boolean.opBoolean","MERGE",FACE,{"derivedFrom":[makeQuery(id+"F7.boolean.opBoolean","MERGE",FACE,{"derivedFrom":[makeQuery(id+"F6.boolean.opBoolean","MERGE",FACE,{"derivedFrom":[makeQuery(id+"F2.boolean.opBoolean","MERGE",FACE,{"derivedFrom":[makeQuery(id+"F1.opExtrude","CAP_FACE",FACE,{"disambiguationData":[OSD([subQ11,subQ23,subQ27,sQuery(id+"F0.wireOp",EDGE,"E2.right"),subQ0])],"isStart":false}),makeQuery(id+"F2.opExtrude","CAP_FACE",FACE,{"disambiguationData":[OSD([subQ11,subQ27,subQ4,subQ0])],"isStart":false})]}),makeQuery(id+"F5.boolean.opBoolean","MERGE",FACE,{"derivedFrom":[makeQuery(id+"F4.boolean.opBoolean","MERGE",FACE,{"derivedFrom":[makeQuery(id+"F2.boolean.opBoolean","MERGE",FACE,{"derivedFrom":[makeQuery(id+"F1.opExtrude","CAP_FACE",FACE,{"disambiguationData":[OSD([subQ24,sQuery(id+"F0.wireOp",EDGE,"E1.top"),subQ26,sQuery(id+"F0.wireOp",EDGE,"E1.right"),subQ25])],"isStart":false}),makeQuery(id+"F2.opExtrude","CAP_FACE",FACE,{"disambiguationData":[OSD([subQ11,subQ26,subQ25,sQuery(id+"F0.wireOp",EDGE,"E53"),subQ0])],"isStart":false})]}),makeQuery(id+"F4.opExtrude","CAP_FACE",FACE,{"disambiguationData":[OSD([subQ11,subQ16,subQ5,subQ8,subQ20,subQ19,subQ22,subQ21,subQ13,subQ12,subQ18,subQ17,subQ15,subQ14])],"isStart":false})]}),makeQuery(id+"F5.opExtrude","CAP_FACE",FACE,{"disambiguationData":[OSD([subQ24,subQ23,subQ10,subQ16,subQ7,sQuery(id+"F0.wireOp",EDGE,"E29.0"),sQuery(id+"F0.wireOp",EDGE,"E30"),sQuery(id+"F0.wireOp",EDGE,"E31.0")])],"isStart":false})]}),makeQuery(id+"F6.opExtrude","CAP_FACE",FACE,{"disambiguationData":[OSD([subQ11,subQ22,subQ21,sQuery(id+"F0.wireOp",EDGE,"E41.0"),sQuery(id+"F0.wireOp",EDGE,"E42.0")])],"isStart":false}),makeQuery(id+"F6.opExtrude","CAP_FACE",FACE,{"disambiguationData":[OSD([subQ11,subQ20,subQ19,sQuery(id+"F0.wireOp",EDGE,"E43.0"),sQuery(id+"F0.wireOp",EDGE,"E44.0")])],"isStart":false}),makeQuery(id+"F6.opExtrude","CAP_FACE",FACE,{"disambiguationData":[OSD([subQ16,subQ18,subQ17,sQuery(id+"F0.wireOp",EDGE,"E39.0"),sQuery(id+"F0.wireOp",EDGE,"E40.0")])],"isStart":false}),makeQuery(id+"F6.opExtrude","CAP_FACE",FACE,{"disambiguationData":[OSD([subQ16,subQ15,subQ14,sQuery(id+"F0.wireOp",EDGE,"E37.0"),sQuery(id+"F0.wireOp",EDGE,"E38.0")])],"isStart":false})]}),makeQuery(id+"F7.opExtrude","CAP_FACE",FACE,{"disambiguationData":[OSD([subQ11,subQ13,subQ12,sQuery(id+"F0.wireOp",EDGE,"E48.0"),sQuery(id+"F0.wireOp",EDGE,"E49.0")])],"isStart":false})]}),makeQuery(id+"F8.opExtrude","CAP_FACE",FACE,{"disambiguationData":[OSD([subQ11,subQ10,subQ9,sQuery(id+"F0.wireOp",EDGE,"E51.0")])],"isStart":false}),makeQuery(id+"F8.opExtrude","CAP_FACE",FACE,{"disambiguationData":[OSD([subQ11,subQ7,subQ6,sQuery(id+"F0.wireOp",EDGE,"E50.0")])],"isStart":false})]}),makeQuery(id+"F9.opExtrude","CAP_FACE",FACE,{"disambiguationData":[OSD([subQ10,subQ9,subQ8,sQuery(id+"F0.wireOp",EDGE,"E52.0")])],"isStart":false})]}),makeQuery(id+"F10.opExtrude","CAP_FACE",FACE,{"disambiguationData":[OSD([subQ7,subQ6,subQ5,sQuery(id+"F0.wireOp",EDGE,"E55.0")])],"isStart":false})]}),makeQuery(id+"F11.opExtrude","CAP_FACE",FACE,{"disambiguationData":[OSD([subQ3,subQ2,subQ1,sQuery(id+"F0.wireOp",EDGE,"E59.0"),sQuery(id+"F0.wireOp",EDGE,"E59.1"),sQuery(id+"F0.wireOp",EDGE,"E59.2"),subQ0])],"isStart":false})]}),makeQuery(id+"F14.opExtrude","SWEPT_FACE",FACE,{"disambiguationData":[OSD([subQ4]),TDD([makeQuery(id+"F2.opExtrude","CAP_EDGE",EDGE,{"disambiguationData":[OSD([subQ4])],"isStart":false})])]})]}),makeQuery(id+"F16.opExtrude","CAP_FACE",FACE,{"disambiguationData":[OSD([subQ3,subQ1,sQuery(id+"F0.wireOp",EDGE,"E60"),sQuery(id+"F0.wireOp",EDGE,"E67.0")])],"isStart":false}),makeQuery(id+"F16.opExtrude","CAP_FACE",FACE,{"disambiguationData":[OSD([subQ2,subQ1,sQuery(id+"F0.wireOp",EDGE,"E63"),sQuery(id+"F0.wireOp",EDGE,"E65.0")])],"isStart":false}),makeQuery(id+"F16.opExtrude","CAP_FACE",FACE,{"disambiguationData":[OSD([subQ1,sQuery(id+"F0.wireOp",EDGE,"E62"),sQuery(id+"F0.wireOp",EDGE,"E64.0"),subQ0])],"isStart":false}),makeQuery(id+"F16.opExtrude","CAP_FACE",FACE,{"disambiguationData":[OSD([subQ1,sQuery(id+"F0.wireOp",EDGE,"E61"),sQuery(id+"F0.wireOp",EDGE,"E66.0"),subQ0])],"isStart":false})]});}
            extrude(context, id + "F17", {"entities" : qUnion([Q0]), "operationType" : NewBodyOperationType.ADD, "endBound" : BoundingType.UP_TO_SURFACE, "depth" : 25.4 * mm, "endBoundEntityFace" : qUnion([Q1]), "offsetDistance" : 25.4 * mm});
        }
        {
            var Q0;
            {var subQ3=sQuery(id+"F0.wireOp",EDGE,"E64.0");var subQ5=sQuery(id+"F0.wireOp",EDGE,"E72");var subQ7=makeQuery(id+"F0.imprint","INTERSECT",VERTEX,{"derivedFrom":[subQ3,subQ5]});Q0=makeQuery(id+"F0.imprint","IMPRINT",FACE,{"disambiguationData":[TD([[makeQuery(id+"F0.imprint","IMPRINT",EDGE,{"disambiguationData":[TD([[subQ7,-1.0]])],"derivedFrom":subQ3}),1.0]])]});}
            var Q1;
            {var subQ2=sQuery(id+"F0.wireOp",EDGE,"E63");Q1=makeQuery(id+"F0.imprint","IMPRINT",FACE,{"disambiguationData":[TD([[makeQuery(id+"F0.imprint","IMPRINT",EDGE,{"derivedFrom":subQ2}),-1.0]])]});}
            var Q2;
            {var subQ2=sQuery(id+"F0.wireOp",EDGE,"E60");Q2=makeQuery(id+"F0.imprint","IMPRINT",FACE,{"disambiguationData":[TD([[makeQuery(id+"F0.imprint","IMPRINT",EDGE,{"derivedFrom":subQ2}),-1.0]])]});}
            var Q3;
            {var subQ0=sQuery(id+"F0.wireOp",EDGE,"E61");Q3=makeQuery(id+"F0.imprint","IMPRINT",FACE,{"disambiguationData":[TD([[makeQuery(id+"F0.imprint","IMPRINT",EDGE,{"derivedFrom":subQ0}),-1.0]])]});}
            var Q4;
            {var subQ0=sQuery(id+"F0.wireOp",EDGE,"E72");var subQ1=sQuery(id+"F0.wireOp",EDGE,"E58");var subQ2=sQuery(id+"F0.wireOp",EDGE,"E57");var subQ3=sQuery(id+"F0.wireOp",EDGE,"E56");var subQ4=sQuery(id+"F0.wireOp",EDGE,"E54");var subQ5=sQuery(id+"F0.wireOp",EDGE,"E20");var subQ6=sQuery(id+"F0.wireOp",EDGE,"E19");var subQ7=sQuery(id+"F0.wireOp",EDGE,"E18");var subQ8=sQuery(id+"F0.wireOp",EDGE,"E22");var subQ9=sQuery(id+"F0.wireOp",EDGE,"E21");var subQ10=sQuery(id+"F0.wireOp",EDGE,"E16");var subQ11=sQuery(id+"F0.wireOp",EDGE,"E0.bottom");var subQ12=sQuery(id+"F0.wireOp",EDGE,"E27.5");var subQ13=sQuery(id+"F0.wireOp",EDGE,"E27.4");var subQ14=sQuery(id+"F0.wireOp",EDGE,"E28.3");var subQ15=sQuery(id+"F0.wireOp",EDGE,"E28.2");var subQ16=sQuery(id+"F0.wireOp",EDGE,"E17");var subQ17=sQuery(id+"F0.wireOp",EDGE,"E28.1");var subQ18=sQuery(id+"F0.wireOp",EDGE,"E28.0");var subQ19=sQuery(id+"F0.wireOp",EDGE,"E27.1");var subQ20=sQuery(id+"F0.wireOp",EDGE,"E27.0");var subQ21=sQuery(id+"F0.wireOp",EDGE,"E27.3");var subQ22=sQuery(id+"F0.wireOp",EDGE,"E27.2");var subQ23=sQuery(id+"F0.wireOp",EDGE,"E2.bottom");var subQ24=sQuery(id+"F0.wireOp",EDGE,"E1.bottom");var subQ25=sQuery(id+"F0.wireOp",EDGE,"E15");var subQ26=sQuery(id+"F0.wireOp",EDGE,"E1.left");var subQ27=sQuery(id+"F0.wireOp",EDGE,"E2.left");Q4=makeQuery(id+"F17.boolean.opBoolean","MERGE",FACE,{"derivedFrom":[makeQuery(id+"F16.boolean.opBoolean","MERGE",FACE,{"derivedFrom":[makeQuery(id+"F14.boolean.opBoolean","MERGE",FACE,{"derivedFrom":[makeQuery(id+"F11.boolean.opBoolean","MERGE",FACE,{"derivedFrom":[makeQuery(id+"F10.boolean.opBoolean","MERGE",FACE,{"derivedFrom":[makeQuery(id+"F9.boolean.opBoolean","MERGE",FACE,{"derivedFrom":[makeQuery(id+"F8.boolean.opBoolean","MERGE",FACE,{"derivedFrom":[makeQuery(id+"F7.boolean.opBoolean","MERGE",FACE,{"derivedFrom":[makeQuery(id+"F6.boolean.opBoolean","MERGE",FACE,{"derivedFrom":[makeQuery(id+"F2.boolean.opBoolean","MERGE",FACE,{"derivedFrom":[makeQuery(id+"F1.opExtrude","CAP_FACE",FACE,{"disambiguationData":[OSD([subQ11,subQ23,subQ27,sQuery(id+"F0.wireOp",EDGE,"E2.right"),subQ0])],"isStart":false}),makeQuery(id+"F2.opExtrude","CAP_FACE",FACE,{"disambiguationData":[OSD([subQ11,subQ27,subQ4,subQ0])],"isStart":false})]}),makeQuery(id+"F5.boolean.opBoolean","MERGE",FACE,{"derivedFrom":[makeQuery(id+"F4.boolean.opBoolean","MERGE",FACE,{"derivedFrom":[makeQuery(id+"F2.boolean.opBoolean","MERGE",FACE,{"derivedFrom":[makeQuery(id+"F1.opExtrude","CAP_FACE",FACE,{"disambiguationData":[OSD([subQ24,sQuery(id+"F0.wireOp",EDGE,"E1.top"),subQ26,sQuery(id+"F0.wireOp",EDGE,"E1.right"),subQ25])],"isStart":false}),makeQuery(id+"F2.opExtrude","CAP_FACE",FACE,{"disambiguationData":[OSD([subQ11,subQ26,subQ25,sQuery(id+"F0.wireOp",EDGE,"E53"),subQ0])],"isStart":false})]}),makeQuery(id+"F4.opExtrude","CAP_FACE",FACE,{"disambiguationData":[OSD([subQ11,subQ16,subQ5,subQ8,subQ20,subQ19,subQ22,subQ21,subQ13,subQ12,subQ18,subQ17,subQ15,subQ14])],"isStart":false})]}),makeQuery(id+"F5.opExtrude","CAP_FACE",FACE,{"disambiguationData":[OSD([subQ24,subQ23,subQ10,subQ16,subQ7,sQuery(id+"F0.wireOp",EDGE,"E29.0"),sQuery(id+"F0.wireOp",EDGE,"E30"),sQuery(id+"F0.wireOp",EDGE,"E31.0")])],"isStart":false})]}),makeQuery(id+"F6.opExtrude","CAP_FACE",FACE,{"disambiguationData":[OSD([subQ11,subQ22,subQ21,sQuery(id+"F0.wireOp",EDGE,"E41.0"),sQuery(id+"F0.wireOp",EDGE,"E42.0")])],"isStart":false}),makeQuery(id+"F6.opExtrude","CAP_FACE",FACE,{"disambiguationData":[OSD([subQ11,subQ20,subQ19,sQuery(id+"F0.wireOp",EDGE,"E43.0"),sQuery(id+"F0.wireOp",EDGE,"E44.0")])],"isStart":false}),makeQuery(id+"F6.opExtrude","CAP_FACE",FACE,{"disambiguationData":[OSD([subQ16,subQ18,subQ17,sQuery(id+"F0.wireOp",EDGE,"E39.0"),sQuery(id+"F0.wireOp",EDGE,"E40.0")])],"isStart":false}),makeQuery(id+"F6.opExtrude","CAP_FACE",FACE,{"disambiguationData":[OSD([subQ16,subQ15,subQ14,sQuery(id+"F0.wireOp",EDGE,"E37.0"),sQuery(id+"F0.wireOp",EDGE,"E38.0")])],"isStart":false})]}),makeQuery(id+"F7.opExtrude","CAP_FACE",FACE,{"disambiguationData":[OSD([subQ11,subQ13,subQ12,sQuery(id+"F0.wireOp",EDGE,"E48.0"),sQuery(id+"F0.wireOp",EDGE,"E49.0")])],"isStart":false})]}),makeQuery(id+"F8.opExtrude","CAP_FACE",FACE,{"disambiguationData":[OSD([subQ11,subQ10,subQ9,sQuery(id+"F0.wireOp",EDGE,"E51.0")])],"isStart":false}),makeQuery(id+"F8.opExtrude","CAP_FACE",FACE,{"disambiguationData":[OSD([subQ11,subQ7,subQ6,sQuery(id+"F0.wireOp",EDGE,"E50.0")])],"isStart":false})]}),makeQuery(id+"F9.opExtrude","CAP_FACE",FACE,{"disambiguationData":[OSD([subQ10,subQ9,subQ8,sQuery(id+"F0.wireOp",EDGE,"E52.0")])],"isStart":false})]}),makeQuery(id+"F10.opExtrude","CAP_FACE",FACE,{"disambiguationData":[OSD([subQ7,subQ6,subQ5,sQuery(id+"F0.wireOp",EDGE,"E55.0")])],"isStart":false})]}),makeQuery(id+"F11.opExtrude","CAP_FACE",FACE,{"disambiguationData":[OSD([subQ3,subQ2,subQ1,sQuery(id+"F0.wireOp",EDGE,"E59.0"),sQuery(id+"F0.wireOp",EDGE,"E59.1"),sQuery(id+"F0.wireOp",EDGE,"E59.2"),subQ0])],"isStart":false})]}),makeQuery(id+"F14.opExtrude","SWEPT_FACE",FACE,{"disambiguationData":[OSD([subQ4]),TDD([makeQuery(id+"F2.opExtrude","CAP_EDGE",EDGE,{"disambiguationData":[OSD([subQ4])],"isStart":false})])]})]}),makeQuery(id+"F16.opExtrude","CAP_FACE",FACE,{"disambiguationData":[OSD([subQ3,subQ1,sQuery(id+"F0.wireOp",EDGE,"E60"),sQuery(id+"F0.wireOp",EDGE,"E67.0")])],"isStart":false}),makeQuery(id+"F16.opExtrude","CAP_FACE",FACE,{"disambiguationData":[OSD([subQ2,subQ1,sQuery(id+"F0.wireOp",EDGE,"E63"),sQuery(id+"F0.wireOp",EDGE,"E65.0")])],"isStart":false}),makeQuery(id+"F16.opExtrude","CAP_FACE",FACE,{"disambiguationData":[OSD([subQ1,sQuery(id+"F0.wireOp",EDGE,"E62"),sQuery(id+"F0.wireOp",EDGE,"E64.0"),subQ0])],"isStart":false}),makeQuery(id+"F16.opExtrude","CAP_FACE",FACE,{"disambiguationData":[OSD([subQ1,sQuery(id+"F0.wireOp",EDGE,"E61"),sQuery(id+"F0.wireOp",EDGE,"E66.0"),subQ0])],"isStart":false})]}),makeQuery(id+"F17.opExtrude","CAP_FACE",FACE,{"disambiguationData":[OSD([subQ1,sQuery(id+"F0.wireOp",EDGE,"E70"),sQuery(id+"F0.wireOp",EDGE,"E71"),subQ0])],"isStart":false})]});}
            extrude(context, id + "F18", {"entities" : qUnion([Q0, Q1, Q2, Q3]), "operationType" : NewBodyOperationType.ADD, "endBound" : BoundingType.UP_TO_SURFACE, "depth" : 25.4 * mm, "endBoundEntityFace" : qUnion([Q4]), "offsetDistance" : 25.4 * mm});
        }
        {
            var Q0;
            Q0=makeQuery(id+"F1.opExtrude","SWEPT_BODY",BODY,{"disambiguationData":[OSD([sQuery(id+"F0.wireOp",EDGE,"E0.bottom"),sQuery(id+"F0.wireOp",EDGE,"E2.bottom"),sQuery(id+"F0.wireOp",EDGE,"E2.left"),sQuery(id+"F0.wireOp",EDGE,"E2.right"),sQuery(id+"F0.wireOp",EDGE,"E72")])]});
            var Q1;
            {var subQ0=sQuery(id+"F0.wireOp",EDGE,"E15");var subQ1=sQuery(id+"F0.wireOp",EDGE,"E1.left");Q1=makeQuery(id+"F2.boolean.opBoolean","MERGE",FACE,{"derivedFrom":[makeQuery(id+"F1.opExtrude","CAP_FACE",FACE,{"disambiguationData":[OSD([sQuery(id+"F0.wireOp",EDGE,"E1.bottom"),sQuery(id+"F0.wireOp",EDGE,"E1.top"),subQ1,sQuery(id+"F0.wireOp",EDGE,"E1.right"),subQ0])],"isStart":true}),makeQuery(id+"F2.opExtrude","CAP_FACE",FACE,{"disambiguationData":[OSD([sQuery(id+"F0.wireOp",EDGE,"E0.bottom"),subQ1,subQ0,sQuery(id+"F0.wireOp",EDGE,"E53"),sQuery(id+"F0.wireOp",EDGE,"E72")])],"isStart":true})]});}
            mirror(context, id + "F19", {"operationType" : NewBodyOperationType.ADD, "entities" : qUnion([Q0]), "mirrorPlane" : qUnion([Q1])});
        }
        {
            var Q0;
            Q0=makeQuery(id+"F12.imprint","IMPRINT",FACE,{"disambiguationData":[TD([[makeQuery(id+"F12.imprint","IMPRINT",EDGE,{"derivedFrom":sQuery(id+"F12.wireOp",EDGE,"E73.bottom")}),-1.0]])]});
            var Q1;
            Q1=makeQuery(id+"F12.imprint","IMPRINT",FACE,{"disambiguationData":[TD([[makeQuery(id+"F12.imprint","IMPRINT",EDGE,{"derivedFrom":sQuery(id+"F12.wireOp",EDGE,"E74.top")}),-1.0]])]});
            var Q2;
            Q2=makeQuery(id+"F12.imprint","IMPRINT",FACE,{"disambiguationData":[TD([[makeQuery(id+"F12.imprint","IMPRINT",EDGE,{"derivedFrom":sQuery(id+"F12.wireOp",EDGE,"E75.bottom")}),-1.0]])]});
            var Q3;
            Q3=makeQuery(id+"F12.imprint","IMPRINT",FACE,{"disambiguationData":[TD([[makeQuery(id+"F12.imprint","IMPRINT",EDGE,{"derivedFrom":sQuery(id+"F12.wireOp",EDGE,"E76.bottom")}),-1.0]])]});
            var Q4;
            Q4=makeQuery(id+"F12.imprint","IMPRINT",FACE,{"disambiguationData":[TD([[makeQuery(id+"F12.imprint","IMPRINT",EDGE,{"derivedFrom":sQuery(id+"F12.wireOp",EDGE,"E77.bottom")}),-1.0]])]});
            extrude(context, id + "F20", {"entities" : qUnion([Q0, Q1, Q2, Q3, Q4]), "operationType" : NewBodyOperationType.ADD, "endBound" : BoundingType.UP_TO_NEXT, "oppositeDirection" : true, "depth" : 25.4 * mm, "offsetDistance" : 25.4 * mm});
        }
        {
            var Q0;
            {var subQ24=sQuery(id+"F0.wireOp",EDGE,"E59.0");Q0=makeQuery(id+"F0.imprint","IMPRINT",FACE,{"disambiguationData":[TD([[makeQuery(id+"F0.imprint","IMPRINT",EDGE,{"derivedFrom":subQ24}),1.0]])]});}
            extrude(context, id + "F21", {"entities" : qUnion([Q0]), "operationType" : NewBodyOperationType.ADD, "endBound" : BoundingType.UP_TO_NEXT, "oppositeDirection" : true, "depth" : 25.4 * mm, "offsetDistance" : 25.4 * mm});
        }
        {
            var Q0;
            {var subQ16=sQuery(id+"F13.wireOp",EDGE,"E78.bottom");Q0=makeQuery(id+"F13.imprint","IMPRINT",FACE,{"disambiguationData":[TD([[makeQuery(id+"F13.imprint","IMPRINT",EDGE,{"derivedFrom":subQ16}),-1.0]])]});}
            var Q1;
            {var subQ1=sQuery(id+"F0.wireOp",EDGE,"E0.bottom");var subQ18=makeQuery(id+"F0.imprint","INTERSECT",VERTEX,{"derivedFrom":[subQ1,sQuery(id+"F0.wireOp",EDGE,"E54")]});var subQ22=sQuery(id+"F0.wireOp",EDGE,"E49.0");var subQ23=makeQuery(id+"F0.imprint","INTERSECT",VERTEX,{"derivedFrom":[subQ1,subQ22]});var subQ24=makeQuery(id+"F0.imprint","IMPRINT",EDGE,{"disambiguationData":[TD([[subQ23,1.0]])],"derivedFrom":subQ1});var subQ25=makeQuery(id+"F0.imprint","IMPRINT",EDGE,{"disambiguationData":[TD([[subQ18,1.0]])],"derivedFrom":subQ1});var subQ28=makeQuery(id+"F3.opExtrude","CAP_EDGE",EDGE,{"disambiguationData":[OSD([subQ1]),TDD([subQ25,subQ24])],"isStart":true});Q1=makeQuery(id+"F13.imprint","IMPRINT",FACE,{"disambiguationData":[TD([[makeQuery(id+"F13.imprint","IMPRINT",EDGE,{"derivedFrom":subQ28}),-1.0]])]});}
            extrude(context, id + "F22", {"entities" : qUnion([Q0, Q1]), "operationType" : NewBodyOperationType.REMOVE, "endBound" : BoundingType.THROUGH_ALL, "oppositeDirection" : true, "depth" : 25.4 * mm, "offsetDistance" : 25.4 * mm});
        }
    });
